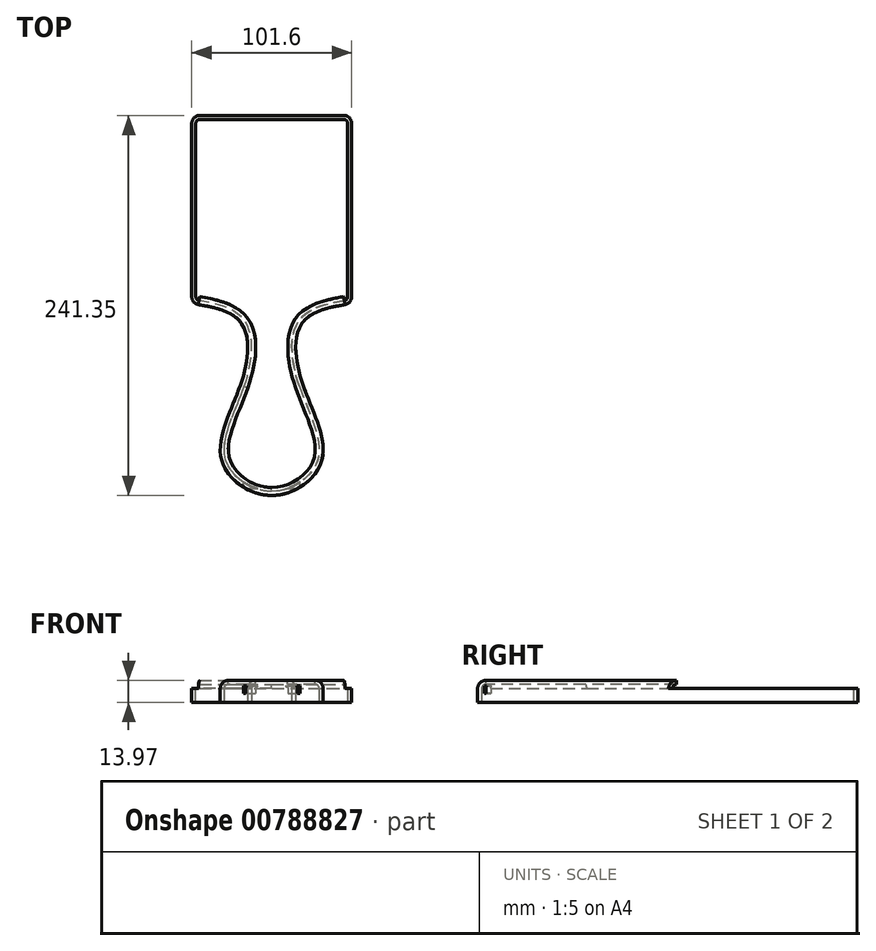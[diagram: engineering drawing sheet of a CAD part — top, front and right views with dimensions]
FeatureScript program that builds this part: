
annotation { "Feature Type Name" : "Feature", "Feature Type Description" : "" }
export const myFeature = defineFeature(function(context is Context, id is Id, definition is map)
    precondition{}
    {
        {
            var Q0;
            Q0=qCreatedBy(makeId("Top.planeOp"),FACE);
            var sketch = newSketch(context, id + "F0", { "sketchPlane" : qUnion([Q0])});
            skLineSegment(sketch, "E0.top", {"start": v(-50.8, -59.7) * mm, "end": v(50.8, -59.7) * mm});
            skLineSegment(sketch, "E1.bottom", {"start": v(-19.05, -59.7) * mm, "end": v(19.05, -59.7) * mm});
            skLineSegment(sketch, "E1.top", {"start": v(-19.05, -143.51) * mm, "end": v(19.05, -143.51) * mm});
            skLineSegment(sketch, "E2", {"start": v(-19.05, -59.69) * mm, "end": v(-138.22, -148.68) * mm, "construction": true});
            skPoint(sketch, "E3.4.internal.snap0", {"position": v(0, -143.51) * mm});
            skFitSpline(sketch, "E4", {"points": [v(31.98, -161.28) * mm, v(-138.22, -161.28) * mm], "startDerivative": vector(-191.75, -9.7) * mm, "endDerivative": vector(-168.23, 0) * mm, "construction": true});
            skFitSpline(sketch, "E5", {"points": [v(19.04, -111.52) * mm, v(-199.9, -111.52) * mm], "startDerivative": vector(-218.94, 0) * mm, "endDerivative": vector(-218.94, 0) * mm, "construction": true});
            skLineSegment(sketch, "E6", {"start": v(50.8, -59.7) * mm, "end": v(50.8, -228.04) * mm, "construction": true});
            skLineSegment(sketch, "E7", {"start": v(-50.8, -59.7) * mm, "end": v(-50.8, -228.04) * mm, "construction": true});
            skPoint(sketch, "E8", {"position": v(-44.45, -162.64) * mm});
            skPoint(sketch, "E9", {"position": v(31.8, -161.3) * mm});
            skLineSegment(sketch, "E10", {"start": v(0, -228.04) * mm, "end": v(0, -135.28) * mm});
            skPoint(sketch, "E11.orphan", {"position": v(0, -221.87) * mm});
            skLineSegment(sketch, "E12", {"start": v(-50.8, -59.7) * mm, "end": v(-50.8, 59.69) * mm});
            skLineSegment(sketch, "E13", {"start": v(-50.8, 59.69) * mm, "end": v(50.8, 59.69) * mm});
            skLineSegment(sketch, "E14", {"start": v(50.8, 59.7) * mm, "end": v(50.8, -59.7) * mm});
            skFitSpline(sketch, "E15", {"points": [v(-50.8, -59.7) * mm, v(-19.83, -71.53) * mm, v(-19.05, -108.97) * mm, v(-31.95, -158.73) * mm, v(0, -181.66) * mm, v(31.95, -158.73) * mm, v(19.05, -108.97) * mm, v(19.83, -71.53) * mm, v(50.8, -59.7) * mm], "startDerivative": vector(328.9, -55.01) * mm, "endDerivative": vector(328.9, 55.01) * mm});
            skFitSpline(sketch, "E16.MirrorCS", {"points": [v(50.8, -59.7) * mm, v(19.83, -71.53) * mm, v(19.05, -108.97) * mm, v(31.95, -158.73) * mm, v(0, -181.66) * mm, v(-31.95, -158.73) * mm, v(-19.05, -108.97) * mm, v(-19.83, -71.53) * mm, v(-50.8, -59.7) * mm], "startDerivative": vector(-328.9, -55.01) * mm, "endDerivative": vector(-328.9, 55.01) * mm});
            skLineSegment(sketch, "E17", {"start": v(0, -59.7) * mm, "end": v(0, 0) * mm, "construction": true});
            skLineSegment(sketch, "E18", {"start": v(-19.9, -111.52) * mm, "end": v(19.9, -111.52) * mm});
            skFitSpline(sketch, "E19", {"points": [v(31.98, -161.28) * mm, v(-138.22, -161.28) * mm], "startDerivative": vector(-191.75, -9.7) * mm, "endDerivative": vector(-168.23, 0) * mm, "construction": true});
            skFitSpline(sketch, "E20", {"points": [v(19.04, -111.52) * mm, v(-199.9, -111.52) * mm], "startDerivative": vector(-218.94, 0) * mm, "endDerivative": vector(-218.94, 0) * mm, "construction": true});
            skLineSegment(sketch, "E21", {"start": v(-50.8, 59.7) * mm, "end": v(50.8, 59.7) * mm});
            skFitSpline(sketch, "E22", {"points": [v(-50.8, -59.7) * mm, v(-19.83, -71.53) * mm, v(-19.05, -108.97) * mm, v(-31.95, -158.73) * mm, v(0, -181.66) * mm, v(31.95, -158.73) * mm, v(19.05, -108.97) * mm, v(19.83, -71.53) * mm, v(50.8, -59.7) * mm], "startDerivative": vector(328.9, -55.01) * mm, "endDerivative": vector(328.9, 55.01) * mm});
            skFitSpline(sketch, "E23.MirrorCS", {"points": [v(50.8, -59.7) * mm, v(19.83, -71.53) * mm, v(19.05, -108.97) * mm, v(31.95, -158.73) * mm, v(0, -181.66) * mm, v(-31.95, -158.73) * mm, v(-19.05, -108.97) * mm, v(-19.83, -71.53) * mm, v(-50.8, -59.7) * mm], "startDerivative": vector(-328.9, -55.01) * mm, "endDerivative": vector(-328.9, 55.01) * mm});
            skFitSpline(sketch, "E24", {"points": [v(-20.16, -129.65) * mm, v(-15.25, -116.48) * mm, v(-19.9, -111.52) * mm], "startDerivative": vector(14.14, 25.35) * mm, "endDerivative": vector(-15.4, 9.99) * mm});
            skFitSpline(sketch, "E25.MirrorCS", {"points": [v(20.16, -129.65) * mm, v(15.25, -116.48) * mm, v(19.9, -111.52) * mm], "startDerivative": vector(-14.14, 25.35) * mm, "endDerivative": vector(15.4, 9.99) * mm});
            skArc(sketch, "E26", {"start": v(-20.16, -129.65) * mm, "mid": v(0, -167.4) * mm, "end": v(20.16, -129.65) * mm});
            skSolve(sketch);
        }
        {
            var Q0;
            Q0 = qSketchRegion(id + "F0", true);
            extrude(context, id + "F1", {"entities" : qUnion([Q0]), "depth" : 19.05 * mm, "offsetDistance" : 25.4 * mm});
        }
        {
            var Q0;
            {var subQ0=sQuery(id+"F0.wireOp",EDGE,"619c9e35-8e4e-45b5-954f-d986f7143fad");Q0=makeQuery(id+"F1.opExtrude","CAP_EDGE",EDGE,{"disambiguationData":[OSD([subQ0]),TDD([makeQuery(id+"F0.imprint","IMPRINT",EDGE,{"disambiguationData":[TD([[makeQuery(id+"F0.imprint","INTERSECT",VERTEX,{"disambiguationData":[OD(0.0)],"derivedFrom":[sQuery(id+"F0.wireOp",EDGE,"cb9e0b87-6c60-422b-916c-469ffb9c9941.left"),subQ0]}),-1.0]])],"derivedFrom":subQ0})])],"isStart":false});}
            var Q1;
            {var subQ0=sQuery(id+"F0.wireOp",EDGE,"619c9e35-8e4e-45b5-954f-d986f7143fad");Q1=makeQuery(id+"F1.opExtrude","CAP_EDGE",EDGE,{"disambiguationData":[OSD([subQ0]),TDD([makeQuery(id+"F0.imprint","IMPRINT",EDGE,{"disambiguationData":[TD([[makeQuery(id+"F0.imprint","INTERSECT",VERTEX,{"disambiguationData":[OD(0.0)],"derivedFrom":[sQuery(id+"F0.wireOp",EDGE,"cb9e0b87-6c60-422b-916c-469ffb9c9941.right"),subQ0]}),1.0]])],"derivedFrom":subQ0})])],"isStart":false});}
            var Q2;
            {var subQ0=sQuery(id+"F0.wireOp",EDGE,"619c9e35-8e4e-45b5-954f-d986f7143fad");Q2=makeQuery(id+"F1.opExtrude","CAP_EDGE",EDGE,{"disambiguationData":[OSD([subQ0]),TDD([makeQuery(id+"F0.imprint","IMPRINT",EDGE,{"disambiguationData":[TD([[makeQuery(id+"F0.imprint","INTERSECT",VERTEX,{"disambiguationData":[OD(1.0)],"derivedFrom":[sQuery(id+"F0.wireOp",EDGE,"cb9e0b87-6c60-422b-916c-469ffb9c9941.left"),subQ0]}),1.0]])],"derivedFrom":subQ0})])],"isStart":false});}
            var Q3;
            Q3=makeQuery(id+"F1.opExtrude","CAP_EDGE",EDGE,{"disambiguationData":[OSD([sQuery(id+"F0.wireOp",EDGE,"cb9e0b87-6c60-422b-916c-469ffb9c9941.right")])],"isStart":false});
            var Q4;
            Q4=makeQuery(id+"F1.opExtrude","CAP_EDGE",EDGE,{"disambiguationData":[OSD([sQuery(id+"F0.wireOp",EDGE,"cb9e0b87-6c60-422b-916c-469ffb9c9941.left")])],"isStart":false});
            var Q5;
            Q5=makeQuery(id+"F1.opExtrude","CAP_EDGE",EDGE,{"disambiguationData":[OSD([sQuery(id+"F0.wireOp",EDGE,"abbb529c-c2db-4c8d-9435-7b284728a9ef.right")])],"isStart":false});
            var Q6;
            Q6=makeQuery(id+"F1.opExtrude","CAP_EDGE",EDGE,{"disambiguationData":[OSD([sQuery(id+"F0.wireOp",EDGE,"abbb529c-c2db-4c8d-9435-7b284728a9ef.left")])],"isStart":false});
            var Q7;
            Q7=makeQuery(id+"F1.opExtrude","CAP_EDGE",EDGE,{"disambiguationData":[OSD([sQuery(id+"F0.wireOp",EDGE,"abbb529c-c2db-4c8d-9435-7b284728a9ef.bottom")])],"isStart":false});
            var Q8;
            {var subQ0=sQuery(id+"F0.wireOp",EDGE,"619c9e35-8e4e-45b5-954f-d986f7143fad");Q8=makeQuery(id+"F1.opExtrude","CAP_EDGE",EDGE,{"disambiguationData":[OSD([subQ0]),TDD([makeQuery(id+"F0.imprint","IMPRINT",EDGE,{"disambiguationData":[TD([[makeQuery(id+"F0.imprint","INTERSECT",VERTEX,{"disambiguationData":[OD(1.0)],"derivedFrom":[sQuery(id+"F0.wireOp",EDGE,"cb9e0b87-6c60-422b-916c-469ffb9c9941.left"),subQ0]}),1.0]])],"derivedFrom":subQ0})])],"isStart":true});}
            var Q9;
            {var subQ0=sQuery(id+"F0.wireOp",EDGE,"619c9e35-8e4e-45b5-954f-d986f7143fad");Q9=makeQuery(id+"F1.opExtrude","CAP_EDGE",EDGE,{"disambiguationData":[OSD([subQ0]),TDD([makeQuery(id+"F0.imprint","IMPRINT",EDGE,{"disambiguationData":[TD([[makeQuery(id+"F0.imprint","INTERSECT",VERTEX,{"disambiguationData":[OD(0.0)],"derivedFrom":[sQuery(id+"F0.wireOp",EDGE,"cb9e0b87-6c60-422b-916c-469ffb9c9941.left"),subQ0]}),-1.0]])],"derivedFrom":subQ0})])],"isStart":true});}
            var Q10;
            Q10=makeQuery(id+"F1.opExtrude","CAP_EDGE",EDGE,{"disambiguationData":[OSD([sQuery(id+"F0.wireOp",EDGE,"abbb529c-c2db-4c8d-9435-7b284728a9ef.bottom")])],"isStart":true});
            var Q11;
            {var subQ0=sQuery(id+"F0.wireOp",EDGE,"619c9e35-8e4e-45b5-954f-d986f7143fad");Q11=makeQuery(id+"F1.opExtrude","CAP_EDGE",EDGE,{"disambiguationData":[OSD([subQ0]),TDD([makeQuery(id+"F0.imprint","IMPRINT",EDGE,{"disambiguationData":[TD([[makeQuery(id+"F0.imprint","INTERSECT",VERTEX,{"disambiguationData":[OD(0.0)],"derivedFrom":[sQuery(id+"F0.wireOp",EDGE,"cb9e0b87-6c60-422b-916c-469ffb9c9941.right"),subQ0]}),1.0]])],"derivedFrom":subQ0})])],"isStart":true});}
            var Q12;
            Q12=makeQuery(id+"F1.opExtrude","SWEPT_EDGE",EDGE,{"disambiguationData":[OSD([sQuery(id+"F0.wireOp",EDGE,"abbb529c-c2db-4c8d-9435-7b284728a9ef.top"),sQuery(id+"F0.wireOp",EDGE,"abbb529c-c2db-4c8d-9435-7b284728a9ef.right"),sQuery(id+"F0.wireOp",EDGE,"619c9e35-8e4e-45b5-954f-d986f7143fad")])]});
            var Q13;
            Q13=makeQuery(id+"F1.opExtrude","SWEPT_EDGE",EDGE,{"disambiguationData":[OSD([sQuery(id+"F0.wireOp",EDGE,"abbb529c-c2db-4c8d-9435-7b284728a9ef.top"),sQuery(id+"F0.wireOp",EDGE,"abbb529c-c2db-4c8d-9435-7b284728a9ef.left"),sQuery(id+"F0.wireOp",EDGE,"619c9e35-8e4e-45b5-954f-d986f7143fad")])]});
            var Q14;
            Q14=makeQuery(id+"F1.opExtrude","SWEPT_EDGE",EDGE,{"disambiguationData":[OSD([sQuery(id+"F0.wireOp",EDGE,"abbb529c-c2db-4c8d-9435-7b284728a9ef.bottom"),sQuery(id+"F0.wireOp",EDGE,"abbb529c-c2db-4c8d-9435-7b284728a9ef.left")])]});
            var Q15;
            {var subQ0=sQuery(id+"F0.wireOp",EDGE,"619c9e35-8e4e-45b5-954f-d986f7143fad");var subQ1=sQuery(id+"F0.wireOp",EDGE,"cb9e0b87-6c60-422b-916c-469ffb9c9941.left");Q15=makeQuery(id+"F1.opExtrude","SWEPT_EDGE",EDGE,{"disambiguationData":[OSD([subQ1,subQ0]),TDD([makeQuery(id+"F0.imprint","INTERSECT",VERTEX,{"disambiguationData":[OD(0.0)],"derivedFrom":[subQ1,subQ0]})])]});}
            var Q16;
            {var subQ0=sQuery(id+"F0.wireOp",EDGE,"619c9e35-8e4e-45b5-954f-d986f7143fad");var subQ1=sQuery(id+"F0.wireOp",EDGE,"cb9e0b87-6c60-422b-916c-469ffb9c9941.left");Q16=makeQuery(id+"F1.opExtrude","SWEPT_EDGE",EDGE,{"disambiguationData":[OSD([subQ1,subQ0]),TDD([makeQuery(id+"F0.imprint","INTERSECT",VERTEX,{"disambiguationData":[OD(1.0)],"derivedFrom":[subQ1,subQ0]})])]});}
            var Q17;
            Q17=makeQuery(id+"F1.opExtrude","CAP_EDGE",EDGE,{"disambiguationData":[OSD([sQuery(id+"F0.wireOp",EDGE,"abbb529c-c2db-4c8d-9435-7b284728a9ef.right")])],"isStart":true});
            var Q18;
            Q18=makeQuery(id+"F1.opExtrude","CAP_EDGE",EDGE,{"disambiguationData":[OSD([sQuery(id+"F0.wireOp",EDGE,"abbb529c-c2db-4c8d-9435-7b284728a9ef.left")])],"isStart":true});
            var Q19;
            {var subQ0=sQuery(id+"F0.wireOp",EDGE,"619c9e35-8e4e-45b5-954f-d986f7143fad");var subQ1=sQuery(id+"F0.wireOp",EDGE,"cb9e0b87-6c60-422b-916c-469ffb9c9941.right");Q19=makeQuery(id+"F1.opExtrude","SWEPT_EDGE",EDGE,{"disambiguationData":[OSD([subQ1,subQ0]),TDD([makeQuery(id+"F0.imprint","INTERSECT",VERTEX,{"disambiguationData":[OD(0.0)],"derivedFrom":[subQ1,subQ0]})])]});}
            var Q20;
            {var subQ0=sQuery(id+"F0.wireOp",EDGE,"619c9e35-8e4e-45b5-954f-d986f7143fad");var subQ1=sQuery(id+"F0.wireOp",EDGE,"cb9e0b87-6c60-422b-916c-469ffb9c9941.right");Q20=makeQuery(id+"F1.opExtrude","SWEPT_EDGE",EDGE,{"disambiguationData":[OSD([subQ1,subQ0]),TDD([makeQuery(id+"F0.imprint","INTERSECT",VERTEX,{"disambiguationData":[OD(1.0)],"derivedFrom":[subQ1,subQ0]})])]});}
            var Q21;
            Q21=makeQuery(id+"F1.opExtrude","CAP_EDGE",EDGE,{"disambiguationData":[OSD([sQuery(id+"F0.wireOp",EDGE,"cb9e0b87-6c60-422b-916c-469ffb9c9941.right")])],"isStart":true});
            var Q22;
            Q22=makeQuery(id+"F1.opExtrude","CAP_EDGE",EDGE,{"disambiguationData":[OSD([sQuery(id+"F0.wireOp",EDGE,"cb9e0b87-6c60-422b-916c-469ffb9c9941.left")])],"isStart":true});
            var Q23;
            Q23=makeQuery(id+"F1.opExtrude","SWEPT_EDGE",EDGE,{"disambiguationData":[OSD([sQuery(id+"F0.wireOp",EDGE,"abbb529c-c2db-4c8d-9435-7b284728a9ef.bottom"),sQuery(id+"F0.wireOp",EDGE,"abbb529c-c2db-4c8d-9435-7b284728a9ef.right")])]});
            var Q24;
            Q24=makeQuery(id+"F1.opExtrude","CAP_EDGE",EDGE,{"disambiguationData":[OSD([sQuery(id+"F0.wireOp",EDGE,"4c9936b5-c191-433f-b99c-079e70b91c7e.right")])],"isStart":false});
            var Q25;
            Q25=makeQuery(id+"F1.opExtrude","CAP_EDGE",EDGE,{"disambiguationData":[OSD([sQuery(id+"F0.wireOp",EDGE,"bdb519ba-7cbe-487b-a66f-37edebb15bfe.MirrorCS")])],"isStart":false});
            var Q26;
            Q26=makeQuery(id+"F1.opExtrude","SWEPT_EDGE",EDGE,{"disambiguationData":[OSD([sQuery(id+"F0.wireOp",EDGE,"4c9936b5-c191-433f-b99c-079e70b91c7e.bottom"),sQuery(id+"F0.wireOp",EDGE,"4c9936b5-c191-433f-b99c-079e70b91c7e.right")])]});
            var Q27;
            Q27=makeQuery(id+"F1.opExtrude","CAP_EDGE",EDGE,{"disambiguationData":[OSD([sQuery(id+"F0.wireOp",EDGE,"4c9936b5-c191-433f-b99c-079e70b91c7e.bottom")])],"isStart":false});
            var Q28;
            Q28=makeQuery(id+"F1.opExtrude","CAP_EDGE",EDGE,{"disambiguationData":[OSD([sQuery(id+"F0.wireOp",EDGE,"4c9936b5-c191-433f-b99c-079e70b91c7e.left")])],"isStart":false});
            var Q29;
            Q29=makeQuery(id+"F1.opExtrude","CAP_EDGE",EDGE,{"disambiguationData":[OSD([sQuery(id+"F0.wireOp",EDGE,"2c6a8658-700c-4ae6-8bb7-a65d1a4c6f69")])],"isStart":false});
            var Q30;
            Q30=makeQuery(id+"F1.opExtrude","CAP_EDGE",EDGE,{"disambiguationData":[OSD([sQuery(id+"F0.wireOp",EDGE,"4c9936b5-c191-433f-b99c-079e70b91c7e.right")])],"isStart":true});
            var Q31;
            Q31=makeQuery(id+"F1.opExtrude","SWEPT_EDGE",EDGE,{"disambiguationData":[OSD([sQuery(id+"F0.wireOp",EDGE,"4c9936b5-c191-433f-b99c-079e70b91c7e.top"),sQuery(id+"F0.wireOp",EDGE,"4c9936b5-c191-433f-b99c-079e70b91c7e.right"),sQuery(id+"F0.wireOp",EDGE,"bdb519ba-7cbe-487b-a66f-37edebb15bfe.MirrorCS")])]});
            var Q32;
            Q32=makeQuery(id+"F1.opExtrude","CAP_FACE",FACE,{"disambiguationData":[OSD([sQuery(id+"F0.wireOp",EDGE,"4c9936b5-c191-433f-b99c-079e70b91c7e.bottom"),sQuery(id+"F0.wireOp",EDGE,"4c9936b5-c191-433f-b99c-079e70b91c7e.left"),sQuery(id+"F0.wireOp",EDGE,"4c9936b5-c191-433f-b99c-079e70b91c7e.right"),sQuery(id+"F0.wireOp",EDGE,"2c6a8658-700c-4ae6-8bb7-a65d1a4c6f69"),sQuery(id+"F0.wireOp",EDGE,"bdb519ba-7cbe-487b-a66f-37edebb15bfe.MirrorCS")])],"isStart":true});
            var Q33;
            Q33=makeQuery(id+"F1.opExtrude","SWEPT_EDGE",EDGE,{"disambiguationData":[OSD([sQuery(id+"F0.wireOp",EDGE,"4c9936b5-c191-433f-b99c-079e70b91c7e.bottom"),sQuery(id+"F0.wireOp",EDGE,"4c9936b5-c191-433f-b99c-079e70b91c7e.left")])]});
            var Q34;
            Q34=makeQuery(id+"F1.opExtrude","SWEPT_EDGE",EDGE,{"disambiguationData":[OSD([sQuery(id+"F0.wireOp",EDGE,"4c9936b5-c191-433f-b99c-079e70b91c7e.top"),sQuery(id+"F0.wireOp",EDGE,"4c9936b5-c191-433f-b99c-079e70b91c7e.left"),sQuery(id+"F0.wireOp",EDGE,"2c6a8658-700c-4ae6-8bb7-a65d1a4c6f69")])]});
            var Q35;
            Q35=makeQuery(id+"F1.opExtrude","SWEPT_EDGE",EDGE,{"disambiguationData":[OSD([sQuery(id+"F0.wireOp",EDGE,"2c6a8658-700c-4ae6-8bb7-a65d1a4c6f69"),sQuery(id+"F0.wireOp",EDGE,"bdb519ba-7cbe-487b-a66f-37edebb15bfe.MirrorCS")])]});
            var Q36;
            Q36=makeQuery(id+"F1.opExtrude","SWEPT_EDGE",EDGE,{"disambiguationData":[OSD([sQuery(id+"F0.wireOp",EDGE,"c34ce0ff-0ec7-4ae9-b71e-ae422a1ad343"),sQuery(id+"F0.wireOp",EDGE,"30933a0e-8d92-4604-b30c-e4b37162de66")])]});
            var Q37;
            Q37=makeQuery(id+"F1.opExtrude","CAP_EDGE",EDGE,{"disambiguationData":[OSD([sQuery(id+"F0.wireOp",EDGE,"30933a0e-8d92-4604-b30c-e4b37162de66")])],"isStart":false});
            var Q38;
            Q38=makeQuery(id+"F1.opExtrude","CAP_EDGE",EDGE,{"disambiguationData":[OSD([sQuery(id+"F0.wireOp",EDGE,"c34ce0ff-0ec7-4ae9-b71e-ae422a1ad343")])],"isStart":false});
            var Q39;
            Q39=makeQuery(id+"F1.opExtrude","CAP_EDGE",EDGE,{"disambiguationData":[OSD([sQuery(id+"F0.wireOp",EDGE,"c34ce0ff-0ec7-4ae9-b71e-ae422a1ad343")])],"isStart":true});
            var Q40;
            Q40=makeQuery(id+"F1.opExtrude","CAP_EDGE",EDGE,{"disambiguationData":[OSD([sQuery(id+"F0.wireOp",EDGE,"30933a0e-8d92-4604-b30c-e4b37162de66")])],"isStart":true});
            var Q41;
            Q41=makeQuery(id+"F1.opExtrude","CAP_EDGE",EDGE,{"disambiguationData":[OSD([sQuery(id+"F0.wireOp",EDGE,"5cded980-a9cc-4845-a9e5-2a2afa72b9e1.MirrorCS")])],"isStart":true});
            var Q42;
            Q42=makeQuery(id+"F1.opExtrude","SWEPT_EDGE",EDGE,{"disambiguationData":[OSD([sQuery(id+"F0.wireOp",EDGE,"e66cdaa8-c890-470a-b91a-6813027ddbfc.top"),sQuery(id+"F0.wireOp",EDGE,"dfdcc702-bab6-440e-817f-0e8d2b34580e"),sQuery(id+"F0.wireOp",EDGE,"9f91019e-6544-4331-85e9-98c714eb1747")])]});
            var Q43;
            Q43=makeQuery(id+"F1.opExtrude","CAP_EDGE",EDGE,{"disambiguationData":[OSD([sQuery(id+"F0.wireOp",EDGE,"9f91019e-6544-4331-85e9-98c714eb1747")])],"isStart":true});
            var Q44;
            Q44=makeQuery(id+"F1.opExtrude","CAP_EDGE",EDGE,{"disambiguationData":[OSD([sQuery(id+"F0.wireOp",EDGE,"9f91019e-6544-4331-85e9-98c714eb1747")])],"isStart":false});
            var Q45;
            Q45=makeQuery(id+"F1.opExtrude","SWEPT_EDGE",EDGE,{"disambiguationData":[OSD([sQuery(id+"F0.wireOp",EDGE,"e66cdaa8-c890-470a-b91a-6813027ddbfc.top"),sQuery(id+"F0.wireOp",EDGE,"5cded980-a9cc-4845-a9e5-2a2afa72b9e1.MirrorCS"),sQuery(id+"F0.wireOp",EDGE,"30933a0e-8d92-4604-b30c-e4b37162de66")])]});
            var Q46;
            Q46=makeQuery(id+"F1.opExtrude","CAP_EDGE",EDGE,{"disambiguationData":[OSD([sQuery(id+"F0.wireOp",EDGE,"dfdcc702-bab6-440e-817f-0e8d2b34580e")])],"isStart":true});
            var Q47;
            Q47=makeQuery(id+"F1.opExtrude","CAP_EDGE",EDGE,{"disambiguationData":[OSD([sQuery(id+"F0.wireOp",EDGE,"5cded980-a9cc-4845-a9e5-2a2afa72b9e1.MirrorCS")])],"isStart":false});
            var Q48;
            Q48=makeQuery(id+"F1.opExtrude","CAP_EDGE",EDGE,{"disambiguationData":[OSD([sQuery(id+"F0.wireOp",EDGE,"dfdcc702-bab6-440e-817f-0e8d2b34580e")])],"isStart":false});
            var Q49;
            Q49=makeQuery(id+"F1.opExtrude","SWEPT_EDGE",EDGE,{"disambiguationData":[OSD([sQuery(id+"F0.wireOp",EDGE,"9f91019e-6544-4331-85e9-98c714eb1747"),sQuery(id+"F0.wireOp",EDGE,"c34ce0ff-0ec7-4ae9-b71e-ae422a1ad343")])]});
            var Q50;
            Q50=makeQuery(id+"F1.opExtrude","CAP_EDGE",EDGE,{"disambiguationData":[OSD([sQuery(id+"F0.wireOp",EDGE,"74c69ee1-55aa-481c-bcd1-1569f91f6e900.MirrorCS")])],"isStart":false});
            var Q51;
            Q51=makeQuery(id+"F1.opExtrude","CAP_EDGE",EDGE,{"disambiguationData":[OSD([sQuery(id+"F0.wireOp",EDGE,"03ce3f70-f8f5-48b6-817a-86b3da3b079a")])],"isStart":false});
            var Q52;
            Q52=makeQuery(id+"F1.opExtrude","CAP_EDGE",EDGE,{"disambiguationData":[OSD([sQuery(id+"F0.wireOp",EDGE,"7e58dfbd-d96a-4cb8-ae05-f5717cad55f7")])],"isStart":false});
            var Q53;
            Q53=makeQuery(id+"F1.opExtrude","CAP_EDGE",EDGE,{"disambiguationData":[OSD([sQuery(id+"F0.wireOp",EDGE,"be0bfd59-5de7-4c36-b741-230e249a2633")])],"isStart":false});
            var Q54;
            Q54=makeQuery(id+"F1.opExtrude","CAP_EDGE",EDGE,{"disambiguationData":[OSD([sQuery(id+"F0.wireOp",EDGE,"bf2bad3a-775d-4bb9-9518-0aa501403ff7")])],"isStart":false});
            var Q55;
            Q55=makeQuery(id+"F1.opExtrude","CAP_EDGE",EDGE,{"disambiguationData":[OSD([sQuery(id+"F0.wireOp",EDGE,"74c69ee1-55aa-481c-bcd1-1569f91f6e900.MirrorCS")])],"isStart":true});
            var Q56;
            Q56=makeQuery(id+"F1.opExtrude","CAP_EDGE",EDGE,{"disambiguationData":[OSD([sQuery(id+"F0.wireOp",EDGE,"03ce3f70-f8f5-48b6-817a-86b3da3b079a")])],"isStart":true});
            var Q57;
            Q57=makeQuery(id+"F1.opExtrude","CAP_EDGE",EDGE,{"disambiguationData":[OSD([sQuery(id+"F0.wireOp",EDGE,"7e58dfbd-d96a-4cb8-ae05-f5717cad55f7")])],"isStart":true});
            var Q58;
            Q58=makeQuery(id+"F1.opExtrude","CAP_EDGE",EDGE,{"disambiguationData":[OSD([sQuery(id+"F0.wireOp",EDGE,"be0bfd59-5de7-4c36-b741-230e249a2633")])],"isStart":true});
            var Q59;
            Q59=makeQuery(id+"F1.opExtrude","SWEPT_EDGE",EDGE,{"disambiguationData":[OSD([sQuery(id+"F0.wireOp",EDGE,"c97fd30b-f4b9-4084-8bae-b5abf99d8afd.top"),sQuery(id+"F0.wireOp",EDGE,"03ce3f70-f8f5-48b6-817a-86b3da3b079a"),sQuery(id+"F0.wireOp",EDGE,"74c69ee1-55aa-481c-bcd1-1569f91f6e900.MirrorCS")])]});
            var Q60;
            Q60=makeQuery(id+"F1.opExtrude","SWEPT_EDGE",EDGE,{"disambiguationData":[OSD([sQuery(id+"F0.wireOp",EDGE,"be0bfd59-5de7-4c36-b741-230e249a2633"),sQuery(id+"F0.wireOp",EDGE,"03ce3f70-f8f5-48b6-817a-86b3da3b079a")])]});
            var Q61;
            Q61=makeQuery(id+"F1.opExtrude","SWEPT_EDGE",EDGE,{"disambiguationData":[OSD([sQuery(id+"F0.wireOp",EDGE,"7e58dfbd-d96a-4cb8-ae05-f5717cad55f7"),sQuery(id+"F0.wireOp",EDGE,"be0bfd59-5de7-4c36-b741-230e249a2633")])]});
            var Q62;
            Q62=makeQuery(id+"F1.opExtrude","SWEPT_EDGE",EDGE,{"disambiguationData":[OSD([sQuery(id+"F0.wireOp",EDGE,"c97fd30b-f4b9-4084-8bae-b5abf99d8afd.top"),sQuery(id+"F0.wireOp",EDGE,"7e58dfbd-d96a-4cb8-ae05-f5717cad55f7"),sQuery(id+"F0.wireOp",EDGE,"bf2bad3a-775d-4bb9-9518-0aa501403ff7")])]});
            var Q63;
            Q63=makeQuery(id+"F1.opExtrude","CAP_EDGE",EDGE,{"disambiguationData":[OSD([sQuery(id+"F0.wireOp",EDGE,"E15"),sQuery(id+"F0.wireOp",EDGE,"E16.MirrorCS")])],"isStart":false});
            var Q64;
            Q64=makeQuery(id+"F1.opExtrude","CAP_FACE",FACE,{"disambiguationData":[OSD([sQuery(id+"F0.wireOp",EDGE,"E12"),sQuery(id+"F0.wireOp",EDGE,"E13"),sQuery(id+"F0.wireOp",EDGE,"E14"),sQuery(id+"F0.wireOp",EDGE,"E15"),sQuery(id+"F0.wireOp",EDGE,"E16.MirrorCS")])],"isStart":false});
            var Q65;
            Q65=makeQuery(id+"F1.opExtrude","CAP_FACE",FACE,{"disambiguationData":[OSD([sQuery(id+"F0.wireOp",EDGE,"E12"),sQuery(id+"F0.wireOp",EDGE,"E13"),sQuery(id+"F0.wireOp",EDGE,"E14"),sQuery(id+"F0.wireOp",EDGE,"E15"),sQuery(id+"F0.wireOp",EDGE,"E16.MirrorCS")])],"isStart":true});
            var Q66;
            Q66=makeQuery(id+"F1.opExtrude","SWEPT_EDGE",EDGE,{"disambiguationData":[OSD([sQuery(id+"F0.wireOp",EDGE,"E13"),sQuery(id+"F0.wireOp",EDGE,"E14")])]});
            var Q67;
            Q67=makeQuery(id+"F1.opExtrude","SWEPT_EDGE",EDGE,{"disambiguationData":[OSD([sQuery(id+"F0.wireOp",EDGE,"E0.top"),sQuery(id+"F0.wireOp",EDGE,"E14"),sQuery(id+"F0.wireOp",EDGE,"E16.MirrorCS")])]});
            var Q68;
            Q68=makeQuery(id+"F1.opExtrude","SWEPT_EDGE",EDGE,{"disambiguationData":[OSD([sQuery(id+"F0.wireOp",EDGE,"E0.top"),sQuery(id+"F0.wireOp",EDGE,"E12"),sQuery(id+"F0.wireOp",EDGE,"E15")])]});
            var Q69;
            Q69=makeQuery(id+"F1.opExtrude","SWEPT_EDGE",EDGE,{"disambiguationData":[OSD([sQuery(id+"F0.wireOp",EDGE,"E12"),sQuery(id+"F0.wireOp",EDGE,"E13")])]});
            var Q70;
            Q70=makeQuery(id+"F1.opExtrude","CAP_EDGE",EDGE,{"disambiguationData":[OSD([sQuery(id+"F0.wireOp",EDGE,"E21")])],"isStart":false});
            var Q71;
            Q71=makeQuery(id+"F1.opExtrude","CAP_EDGE",EDGE,{"disambiguationData":[OSD([sQuery(id+"F0.wireOp",EDGE,"E14")])],"isStart":false});
            var Q72;
            Q72=makeQuery(id+"F1.opExtrude","CAP_EDGE",EDGE,{"disambiguationData":[OSD([sQuery(id+"F0.wireOp",EDGE,"E12")])],"isStart":false});
            var Q73;
            Q73=makeQuery(id+"F1.opExtrude","CAP_EDGE",EDGE,{"disambiguationData":[OSD([sQuery(id+"F0.wireOp",EDGE,"E22")])],"isStart":false});
            var Q74;
            Q74=makeQuery(id+"F1.opExtrude","CAP_EDGE",EDGE,{"disambiguationData":[OSD([sQuery(id+"F0.wireOp",EDGE,"E23.MirrorCS")])],"isStart":false});
            var Q75;
            Q75=makeQuery(id+"F1.opExtrude","CAP_EDGE",EDGE,{"disambiguationData":[OSD([sQuery(id+"F0.wireOp",EDGE,"E26")])],"isStart":false});
            var Q76;
            Q76=makeQuery(id+"F1.opExtrude","CAP_EDGE",EDGE,{"disambiguationData":[OSD([sQuery(id+"F0.wireOp",EDGE,"E23.MirrorCS")])],"isStart":true});
            var Q77;
            Q77=makeQuery(id+"F1.opExtrude","CAP_EDGE",EDGE,{"disambiguationData":[OSD([sQuery(id+"F0.wireOp",EDGE,"E25.MirrorCS")])],"isStart":true});
            var Q78;
            Q78=makeQuery(id+"F1.opExtrude","CAP_EDGE",EDGE,{"disambiguationData":[OSD([sQuery(id+"F0.wireOp",EDGE,"E26")])],"isStart":true});
            var Q79;
            Q79=makeQuery(id+"F1.opExtrude","SWEPT_EDGE",EDGE,{"disambiguationData":[OSD([sQuery(id+"F0.wireOp",EDGE,"E0.top"),sQuery(id+"F0.wireOp",EDGE,"E14"),sQuery(id+"F0.wireOp",EDGE,"E23.MirrorCS")])]});
            var Q80;
            Q80=makeQuery(id+"F1.opExtrude","SWEPT_EDGE",EDGE,{"disambiguationData":[OSD([sQuery(id+"F0.wireOp",EDGE,"E18"),sQuery(id+"F0.wireOp",EDGE,"E23.MirrorCS"),sQuery(id+"F0.wireOp",EDGE,"E25.MirrorCS")])]});
            var Q81;
            Q81=makeQuery(id+"F1.opExtrude","SWEPT_EDGE",EDGE,{"disambiguationData":[OSD([sQuery(id+"F0.wireOp",EDGE,"E25.MirrorCS"),sQuery(id+"F0.wireOp",EDGE,"E26")])]});
            var Q82;
            Q82=makeQuery(id+"F1.opExtrude","SWEPT_EDGE",EDGE,{"disambiguationData":[OSD([sQuery(id+"F0.wireOp",EDGE,"E18"),sQuery(id+"F0.wireOp",EDGE,"E22"),sQuery(id+"F0.wireOp",EDGE,"E24")])]});
            var Q83;
            Q83=makeQuery(id+"F1.opExtrude","CAP_EDGE",EDGE,{"disambiguationData":[OSD([sQuery(id+"F0.wireOp",EDGE,"E24")])],"isStart":true});
            var Q84;
            Q84=makeQuery(id+"F1.opExtrude","SWEPT_EDGE",EDGE,{"disambiguationData":[OSD([sQuery(id+"F0.wireOp",EDGE,"E24"),sQuery(id+"F0.wireOp",EDGE,"E26")])]});
            var Q85;
            Q85=makeQuery(id+"F1.opExtrude","CAP_EDGE",EDGE,{"disambiguationData":[OSD([sQuery(id+"F0.wireOp",EDGE,"E22")])],"isStart":true});
            var Q86;
            Q86=makeQuery(id+"F1.opExtrude","SWEPT_EDGE",EDGE,{"disambiguationData":[OSD([sQuery(id+"F0.wireOp",EDGE,"E0.top"),sQuery(id+"F0.wireOp",EDGE,"E12"),sQuery(id+"F0.wireOp",EDGE,"E22")])]});
            var Q87;
            Q87=makeQuery(id+"F1.opExtrude","CAP_EDGE",EDGE,{"disambiguationData":[OSD([sQuery(id+"F0.wireOp",EDGE,"E12")])],"isStart":true});
            var Q88;
            Q88=makeQuery(id+"F1.opExtrude","SWEPT_EDGE",EDGE,{"disambiguationData":[OSD([sQuery(id+"F0.wireOp",EDGE,"E12"),sQuery(id+"F0.wireOp",EDGE,"E21")])]});
            var Q89;
            Q89=makeQuery(id+"F1.opExtrude","SWEPT_EDGE",EDGE,{"disambiguationData":[OSD([sQuery(id+"F0.wireOp",EDGE,"E21"),sQuery(id+"F0.wireOp",EDGE,"E14")])]});
            var Q90;
            Q90=makeQuery(id+"F1.opExtrude","CAP_EDGE",EDGE,{"disambiguationData":[OSD([sQuery(id+"F0.wireOp",EDGE,"E14")])],"isStart":true});
            var Q91;
            Q91=makeQuery(id+"F1.opExtrude","CAP_EDGE",EDGE,{"disambiguationData":[OSD([sQuery(id+"F0.wireOp",EDGE,"E21")])],"isStart":true});
            fillet(context, id + "F2", {"entities" : qUnion([Q0, Q1, Q2, Q3, Q4, Q5, Q6, Q7, Q8, Q9, Q10, Q11, Q12, Q13, Q14, Q15, Q16, Q17, Q18, Q19, Q20, Q21, Q22, Q23, Q24, Q25, Q26, Q27, Q28, Q29, Q30, Q31, Q32, Q33, Q34, Q35, Q36, Q37, Q38, Q39, Q40, Q41, Q42, Q43, Q44, Q45, Q46, Q47, Q48, Q49, Q50, Q51, Q52, Q53, Q54, Q55, Q56, Q57, Q58, Q59, Q60, Q61, Q62, Q63, Q64, Q65, Q66, Q67, Q68, Q69, Q70, Q71, Q72, Q73, Q74, Q75, Q76, Q77, Q78, Q79, Q80, Q81, Q82, Q83, Q84, Q85, Q86, Q87, Q88, Q89, Q90, Q91]), "radius" : 5.08 * mm, "tangentPropagation" : true, "allowEdgeOverflow" : false});
        }
        {
            var Q0;
            Q0=qCreatedBy(makeId("Top.planeOp"),FACE);
            var sketch = newSketch(context, id + "F3", { "sketchPlane" : qUnion([Q0])});
            skLineSegment(sketch, "E27", {"start": v(-45.62, 55) * mm, "end": v(45.76, 55) * mm});
            skCircle(sketch, "E28", {"center": v(-42.67, 52.68) * mm, "radius": 0.64 * mm});
            skCircle(sketch, "E29.1.0.0", {"center": v(-39.12, 52.68) * mm, "radius": 0.64 * mm});
            skCircle(sketch, "E29.2.0.0", {"center": v(-35.56, 52.68) * mm, "radius": 0.64 * mm});
            skCircle(sketch, "E29.3.0.0", {"center": v(-32, 52.68) * mm, "radius": 0.64 * mm});
            skCircle(sketch, "E29.4.0.0", {"center": v(-28.45, 52.68) * mm, "radius": 0.64 * mm});
            skCircle(sketch, "E29.5.0.0", {"center": v(-24.9, 52.68) * mm, "radius": 0.64 * mm});
            skCircle(sketch, "E29.6.0.0", {"center": v(-21.34, 52.68) * mm, "radius": 0.64 * mm});
            skCircle(sketch, "E29.7.0.0", {"center": v(-17.78, 52.68) * mm, "radius": 0.64 * mm});
            skCircle(sketch, "E29.8.0.0", {"center": v(-14.22, 52.68) * mm, "radius": 0.64 * mm});
            skCircle(sketch, "E29.9.0.0", {"center": v(-10.67, 52.68) * mm, "radius": 0.64 * mm});
            skCircle(sketch, "E29.10.0.0", {"center": v(-7.11, 52.68) * mm, "radius": 0.64 * mm});
            skCircle(sketch, "E29.11.0.0", {"center": v(-3.56, 52.68) * mm, "radius": 0.64 * mm});
            skCircle(sketch, "E29.12.0.0", {"center": v(0, 52.68) * mm, "radius": 0.64 * mm});
            skCircle(sketch, "E29.13.0.0", {"center": v(3.56, 52.68) * mm, "radius": 0.64 * mm});
            skCircle(sketch, "E29.14.0.0", {"center": v(7.11, 52.68) * mm, "radius": 0.64 * mm});
            skCircle(sketch, "E29.15.0.0", {"center": v(10.67, 52.68) * mm, "radius": 0.64 * mm});
            skCircle(sketch, "E29.16.0.0", {"center": v(14.22, 52.68) * mm, "radius": 0.64 * mm});
            skCircle(sketch, "E29.17.0.0", {"center": v(17.78, 52.68) * mm, "radius": 0.64 * mm});
            skCircle(sketch, "E29.18.0.0", {"center": v(21.34, 52.68) * mm, "radius": 0.64 * mm});
            skCircle(sketch, "E29.19.0.0", {"center": v(24.9, 52.68) * mm, "radius": 0.64 * mm});
            skLineSegment(sketch, "E29.direction1", {"start": v(-42.67, 52.68) * mm, "end": v(-39.12, 52.68) * mm, "construction": true});
            skCircle(sketch, "E30.0.20.0", {"center": v(28.45, 52.68) * mm, "radius": 0.64 * mm});
            skCircle(sketch, "E30.0.21.0", {"center": v(32, 52.68) * mm, "radius": 0.64 * mm});
            skCircle(sketch, "E30.0.22.0", {"center": v(35.56, 52.68) * mm, "radius": 0.64 * mm});
            skCircle(sketch, "E30.0.23.0", {"center": v(39.12, 52.68) * mm, "radius": 0.64 * mm});
            skCircle(sketch, "E31.0.24.0", {"center": v(42.67, 52.68) * mm, "radius": 0.64 * mm});
            skCircle(sketch, "E32.1.0.0", {"center": v(39.12, 49.02) * mm, "radius": 0.64 * mm});
            skCircle(sketch, "E32.1.0.1", {"center": v(14.22, 49.02) * mm, "radius": 0.64 * mm});
            skCircle(sketch, "E32.1.0.2", {"center": v(-32, 49.02) * mm, "radius": 0.64 * mm});
            skCircle(sketch, "E32.1.0.3", {"center": v(10.67, 49.02) * mm, "radius": 0.64 * mm});
            skCircle(sketch, "E32.1.0.4", {"center": v(-35.56, 49.02) * mm, "radius": 0.64 * mm});
            skCircle(sketch, "E32.1.0.5", {"center": v(17.78, 49.02) * mm, "radius": 0.64 * mm});
            skCircle(sketch, "E32.1.0.6", {"center": v(3.56, 49.02) * mm, "radius": 0.64 * mm});
            skCircle(sketch, "E32.1.0.7", {"center": v(21.34, 49.02) * mm, "radius": 0.64 * mm});
            skCircle(sketch, "E32.1.0.8", {"center": v(42.67, 49.02) * mm, "radius": 0.64 * mm});
            skCircle(sketch, "E32.1.0.9", {"center": v(-7.11, 49.02) * mm, "radius": 0.64 * mm});
            skCircle(sketch, "E32.1.0.10", {"center": v(-3.56, 49.02) * mm, "radius": 0.64 * mm});
            skCircle(sketch, "E32.1.0.11", {"center": v(-10.67, 49.02) * mm, "radius": 0.64 * mm});
            skCircle(sketch, "E32.1.0.12", {"center": v(-14.22, 49.02) * mm, "radius": 0.64 * mm});
            skCircle(sketch, "E32.1.0.13", {"center": v(-21.34, 49.02) * mm, "radius": 0.64 * mm});
            skCircle(sketch, "E32.1.0.14", {"center": v(-24.9, 49.02) * mm, "radius": 0.64 * mm});
            skCircle(sketch, "E32.1.0.15", {"center": v(-28.45, 49.02) * mm, "radius": 0.64 * mm});
            skCircle(sketch, "E32.1.0.16", {"center": v(28.45, 49.02) * mm, "radius": 0.64 * mm});
            skCircle(sketch, "E32.1.0.17", {"center": v(7.11, 49.02) * mm, "radius": 0.64 * mm});
            skCircle(sketch, "E32.1.0.18", {"center": v(32, 49.02) * mm, "radius": 0.64 * mm});
            skCircle(sketch, "E32.1.0.19", {"center": v(35.56, 49.02) * mm, "radius": 0.64 * mm});
            skCircle(sketch, "E32.1.0.20", {"center": v(-17.78, 49.02) * mm, "radius": 0.64 * mm});
            skCircle(sketch, "E32.1.0.21", {"center": v(0, 49.02) * mm, "radius": 0.64 * mm});
            skCircle(sketch, "E32.1.0.22", {"center": v(24.9, 49.02) * mm, "radius": 0.64 * mm});
            skCircle(sketch, "E32.1.0.23", {"center": v(-42.67, 49.02) * mm, "radius": 0.64 * mm});
            skLineSegment(sketch, "E32.1.0.24", {"start": v(-42.67, 49.02) * mm, "end": v(-39.12, 49.02) * mm, "construction": true});
            skCircle(sketch, "E32.1.0.25", {"center": v(-39.12, 49.02) * mm, "radius": 0.64 * mm});
            skCircle(sketch, "E32.2.0.0", {"center": v(39.12, 45.36) * mm, "radius": 0.64 * mm});
            skCircle(sketch, "E32.2.0.1", {"center": v(14.22, 45.36) * mm, "radius": 0.64 * mm});
            skCircle(sketch, "E32.2.0.2", {"center": v(-32, 45.36) * mm, "radius": 0.64 * mm});
            skCircle(sketch, "E32.2.0.3", {"center": v(10.67, 45.36) * mm, "radius": 0.64 * mm});
            skCircle(sketch, "E32.2.0.4", {"center": v(-35.56, 45.36) * mm, "radius": 0.64 * mm});
            skCircle(sketch, "E32.2.0.5", {"center": v(17.78, 45.36) * mm, "radius": 0.64 * mm});
            skCircle(sketch, "E32.2.0.6", {"center": v(3.56, 45.36) * mm, "radius": 0.64 * mm});
            skCircle(sketch, "E32.2.0.7", {"center": v(21.34, 45.36) * mm, "radius": 0.64 * mm});
            skCircle(sketch, "E32.2.0.8", {"center": v(42.67, 45.36) * mm, "radius": 0.64 * mm});
            skCircle(sketch, "E32.2.0.9", {"center": v(-7.11, 45.36) * mm, "radius": 0.64 * mm});
            skCircle(sketch, "E32.2.0.10", {"center": v(-3.56, 45.36) * mm, "radius": 0.64 * mm});
            skCircle(sketch, "E32.2.0.11", {"center": v(-10.67, 45.36) * mm, "radius": 0.64 * mm});
            skCircle(sketch, "E32.2.0.12", {"center": v(-14.22, 45.36) * mm, "radius": 0.64 * mm});
            skCircle(sketch, "E32.2.0.13", {"center": v(-21.34, 45.36) * mm, "radius": 0.64 * mm});
            skCircle(sketch, "E32.2.0.14", {"center": v(-24.9, 45.36) * mm, "radius": 0.64 * mm});
            skCircle(sketch, "E32.2.0.15", {"center": v(-28.45, 45.36) * mm, "radius": 0.64 * mm});
            skCircle(sketch, "E32.2.0.16", {"center": v(28.45, 45.36) * mm, "radius": 0.64 * mm});
            skCircle(sketch, "E32.2.0.17", {"center": v(7.11, 45.36) * mm, "radius": 0.64 * mm});
            skCircle(sketch, "E32.2.0.18", {"center": v(32, 45.36) * mm, "radius": 0.64 * mm});
            skCircle(sketch, "E32.2.0.19", {"center": v(35.56, 45.36) * mm, "radius": 0.64 * mm});
            skCircle(sketch, "E32.2.0.20", {"center": v(-17.78, 45.36) * mm, "radius": 0.64 * mm});
            skCircle(sketch, "E32.2.0.21", {"center": v(0, 45.36) * mm, "radius": 0.64 * mm});
            skCircle(sketch, "E32.2.0.22", {"center": v(24.9, 45.36) * mm, "radius": 0.64 * mm});
            skCircle(sketch, "E32.2.0.23", {"center": v(-42.67, 45.36) * mm, "radius": 0.64 * mm});
            skLineSegment(sketch, "E32.2.0.24", {"start": v(-42.67, 45.36) * mm, "end": v(-39.12, 45.36) * mm, "construction": true});
            skCircle(sketch, "E32.2.0.25", {"center": v(-39.12, 45.36) * mm, "radius": 0.64 * mm});
            skCircle(sketch, "E32.3.0.0", {"center": v(39.12, 41.7) * mm, "radius": 0.64 * mm});
            skCircle(sketch, "E32.3.0.1", {"center": v(14.22, 41.7) * mm, "radius": 0.64 * mm});
            skCircle(sketch, "E32.3.0.2", {"center": v(-32, 41.7) * mm, "radius": 0.64 * mm});
            skCircle(sketch, "E32.3.0.3", {"center": v(10.67, 41.7) * mm, "radius": 0.64 * mm});
            skCircle(sketch, "E32.3.0.4", {"center": v(-35.56, 41.7) * mm, "radius": 0.64 * mm});
            skCircle(sketch, "E32.3.0.5", {"center": v(17.78, 41.7) * mm, "radius": 0.64 * mm});
            skCircle(sketch, "E32.3.0.6", {"center": v(3.56, 41.7) * mm, "radius": 0.64 * mm});
            skCircle(sketch, "E32.3.0.7", {"center": v(21.34, 41.7) * mm, "radius": 0.64 * mm});
            skCircle(sketch, "E32.3.0.8", {"center": v(42.67, 41.7) * mm, "radius": 0.64 * mm});
            skCircle(sketch, "E32.3.0.9", {"center": v(-7.11, 41.7) * mm, "radius": 0.64 * mm});
            skCircle(sketch, "E32.3.0.10", {"center": v(-3.56, 41.7) * mm, "radius": 0.64 * mm});
            skCircle(sketch, "E32.3.0.11", {"center": v(-10.67, 41.7) * mm, "radius": 0.64 * mm});
            skCircle(sketch, "E32.3.0.12", {"center": v(-14.22, 41.7) * mm, "radius": 0.64 * mm});
            skCircle(sketch, "E32.3.0.13", {"center": v(-21.34, 41.7) * mm, "radius": 0.64 * mm});
            skCircle(sketch, "E32.3.0.14", {"center": v(-24.9, 41.7) * mm, "radius": 0.64 * mm});
            skCircle(sketch, "E32.3.0.15", {"center": v(-28.45, 41.7) * mm, "radius": 0.64 * mm});
            skCircle(sketch, "E32.3.0.16", {"center": v(28.45, 41.7) * mm, "radius": 0.64 * mm});
            skCircle(sketch, "E32.3.0.17", {"center": v(7.11, 41.7) * mm, "radius": 0.64 * mm});
            skCircle(sketch, "E32.3.0.18", {"center": v(32, 41.7) * mm, "radius": 0.64 * mm});
            skCircle(sketch, "E32.3.0.19", {"center": v(35.56, 41.7) * mm, "radius": 0.64 * mm});
            skCircle(sketch, "E32.3.0.20", {"center": v(-17.78, 41.7) * mm, "radius": 0.64 * mm});
            skCircle(sketch, "E32.3.0.21", {"center": v(0, 41.7) * mm, "radius": 0.64 * mm});
            skCircle(sketch, "E32.3.0.22", {"center": v(24.9, 41.7) * mm, "radius": 0.64 * mm});
            skCircle(sketch, "E32.3.0.23", {"center": v(-42.67, 41.7) * mm, "radius": 0.64 * mm});
            skLineSegment(sketch, "E32.3.0.24", {"start": v(-42.67, 41.7) * mm, "end": v(-39.12, 41.7) * mm, "construction": true});
            skCircle(sketch, "E32.3.0.25", {"center": v(-39.12, 41.7) * mm, "radius": 0.64 * mm});
            skCircle(sketch, "E32.4.0.0", {"center": v(39.12, 38.05) * mm, "radius": 0.64 * mm});
            skCircle(sketch, "E32.4.0.1", {"center": v(14.22, 38.05) * mm, "radius": 0.64 * mm});
            skCircle(sketch, "E32.4.0.2", {"center": v(-32, 38.05) * mm, "radius": 0.64 * mm});
            skCircle(sketch, "E32.4.0.3", {"center": v(10.67, 38.05) * mm, "radius": 0.64 * mm});
            skCircle(sketch, "E32.4.0.4", {"center": v(-35.56, 38.05) * mm, "radius": 0.64 * mm});
            skCircle(sketch, "E32.4.0.5", {"center": v(17.78, 38.05) * mm, "radius": 0.64 * mm});
            skCircle(sketch, "E32.4.0.6", {"center": v(3.56, 38.05) * mm, "radius": 0.64 * mm});
            skCircle(sketch, "E32.4.0.7", {"center": v(21.34, 38.05) * mm, "radius": 0.64 * mm});
            skCircle(sketch, "E32.4.0.8", {"center": v(42.67, 38.05) * mm, "radius": 0.64 * mm});
            skCircle(sketch, "E32.4.0.9", {"center": v(-7.11, 38.05) * mm, "radius": 0.64 * mm});
            skCircle(sketch, "E32.4.0.10", {"center": v(-3.56, 38.05) * mm, "radius": 0.64 * mm});
            skCircle(sketch, "E32.4.0.11", {"center": v(-10.67, 38.05) * mm, "radius": 0.64 * mm});
            skCircle(sketch, "E32.4.0.12", {"center": v(-14.22, 38.05) * mm, "radius": 0.64 * mm});
            skCircle(sketch, "E32.4.0.13", {"center": v(-21.34, 38.05) * mm, "radius": 0.64 * mm});
            skCircle(sketch, "E32.4.0.14", {"center": v(-24.9, 38.05) * mm, "radius": 0.64 * mm});
            skCircle(sketch, "E32.4.0.15", {"center": v(-28.45, 38.05) * mm, "radius": 0.64 * mm});
            skCircle(sketch, "E32.4.0.16", {"center": v(28.45, 38.05) * mm, "radius": 0.64 * mm});
            skCircle(sketch, "E32.4.0.17", {"center": v(7.11, 38.05) * mm, "radius": 0.64 * mm});
            skCircle(sketch, "E32.4.0.18", {"center": v(32, 38.05) * mm, "radius": 0.64 * mm});
            skCircle(sketch, "E32.4.0.19", {"center": v(35.56, 38.05) * mm, "radius": 0.64 * mm});
            skCircle(sketch, "E32.4.0.20", {"center": v(-17.78, 38.05) * mm, "radius": 0.64 * mm});
            skCircle(sketch, "E32.4.0.21", {"center": v(0, 38.05) * mm, "radius": 0.64 * mm});
            skCircle(sketch, "E32.4.0.22", {"center": v(24.9, 38.05) * mm, "radius": 0.64 * mm});
            skCircle(sketch, "E32.4.0.23", {"center": v(-42.67, 38.05) * mm, "radius": 0.64 * mm});
            skLineSegment(sketch, "E32.4.0.24", {"start": v(-42.67, 38.05) * mm, "end": v(-39.12, 38.05) * mm, "construction": true});
            skCircle(sketch, "E32.4.0.25", {"center": v(-39.12, 38.05) * mm, "radius": 0.64 * mm});
            skCircle(sketch, "E32.5.0.0", {"center": v(39.12, 34.4) * mm, "radius": 0.64 * mm});
            skCircle(sketch, "E32.5.0.1", {"center": v(14.22, 34.4) * mm, "radius": 0.64 * mm});
            skCircle(sketch, "E32.5.0.2", {"center": v(-32, 34.4) * mm, "radius": 0.64 * mm});
            skCircle(sketch, "E32.5.0.3", {"center": v(10.67, 34.4) * mm, "radius": 0.64 * mm});
            skCircle(sketch, "E32.5.0.4", {"center": v(-35.56, 34.4) * mm, "radius": 0.64 * mm});
            skCircle(sketch, "E32.5.0.5", {"center": v(17.78, 34.4) * mm, "radius": 0.64 * mm});
            skCircle(sketch, "E32.5.0.6", {"center": v(3.56, 34.4) * mm, "radius": 0.64 * mm});
            skCircle(sketch, "E32.5.0.7", {"center": v(21.34, 34.4) * mm, "radius": 0.64 * mm});
            skCircle(sketch, "E32.5.0.8", {"center": v(42.67, 34.4) * mm, "radius": 0.64 * mm});
            skCircle(sketch, "E32.5.0.9", {"center": v(-7.11, 34.4) * mm, "radius": 0.64 * mm});
            skCircle(sketch, "E32.5.0.10", {"center": v(-3.56, 34.4) * mm, "radius": 0.64 * mm});
            skCircle(sketch, "E32.5.0.11", {"center": v(-10.67, 34.4) * mm, "radius": 0.64 * mm});
            skCircle(sketch, "E32.5.0.12", {"center": v(-14.22, 34.4) * mm, "radius": 0.64 * mm});
            skCircle(sketch, "E32.5.0.13", {"center": v(-21.34, 34.4) * mm, "radius": 0.64 * mm});
            skCircle(sketch, "E32.5.0.14", {"center": v(-24.9, 34.4) * mm, "radius": 0.64 * mm});
            skCircle(sketch, "E32.5.0.15", {"center": v(-28.45, 34.4) * mm, "radius": 0.64 * mm});
            skCircle(sketch, "E32.5.0.16", {"center": v(28.45, 34.4) * mm, "radius": 0.64 * mm});
            skCircle(sketch, "E32.5.0.17", {"center": v(7.11, 34.4) * mm, "radius": 0.64 * mm});
            skCircle(sketch, "E32.5.0.18", {"center": v(32, 34.4) * mm, "radius": 0.64 * mm});
            skCircle(sketch, "E32.5.0.19", {"center": v(35.56, 34.4) * mm, "radius": 0.64 * mm});
            skCircle(sketch, "E32.5.0.20", {"center": v(-17.78, 34.4) * mm, "radius": 0.64 * mm});
            skCircle(sketch, "E32.5.0.21", {"center": v(0, 34.4) * mm, "radius": 0.64 * mm});
            skCircle(sketch, "E32.5.0.22", {"center": v(24.9, 34.4) * mm, "radius": 0.64 * mm});
            skCircle(sketch, "E32.5.0.23", {"center": v(-42.67, 34.4) * mm, "radius": 0.64 * mm});
            skLineSegment(sketch, "E32.5.0.24", {"start": v(-42.67, 34.4) * mm, "end": v(-39.12, 34.4) * mm, "construction": true});
            skCircle(sketch, "E32.5.0.25", {"center": v(-39.12, 34.4) * mm, "radius": 0.64 * mm});
            skCircle(sketch, "E32.6.0.0", {"center": v(39.12, 30.73) * mm, "radius": 0.64 * mm});
            skCircle(sketch, "E32.6.0.1", {"center": v(14.22, 30.73) * mm, "radius": 0.64 * mm});
            skCircle(sketch, "E32.6.0.2", {"center": v(-32, 30.73) * mm, "radius": 0.64 * mm});
            skCircle(sketch, "E32.6.0.3", {"center": v(10.67, 30.73) * mm, "radius": 0.64 * mm});
            skCircle(sketch, "E32.6.0.4", {"center": v(-35.56, 30.73) * mm, "radius": 0.64 * mm});
            skCircle(sketch, "E32.6.0.5", {"center": v(17.78, 30.73) * mm, "radius": 0.64 * mm});
            skCircle(sketch, "E32.6.0.6", {"center": v(3.56, 30.73) * mm, "radius": 0.64 * mm});
            skCircle(sketch, "E32.6.0.7", {"center": v(21.34, 30.73) * mm, "radius": 0.64 * mm});
            skCircle(sketch, "E32.6.0.8", {"center": v(42.67, 30.73) * mm, "radius": 0.64 * mm});
            skCircle(sketch, "E32.6.0.9", {"center": v(-7.11, 30.73) * mm, "radius": 0.64 * mm});
            skCircle(sketch, "E32.6.0.10", {"center": v(-3.56, 30.73) * mm, "radius": 0.64 * mm});
            skCircle(sketch, "E32.6.0.11", {"center": v(-10.67, 30.73) * mm, "radius": 0.64 * mm});
            skCircle(sketch, "E32.6.0.12", {"center": v(-14.22, 30.73) * mm, "radius": 0.64 * mm});
            skCircle(sketch, "E32.6.0.13", {"center": v(-21.34, 30.73) * mm, "radius": 0.64 * mm});
            skCircle(sketch, "E32.6.0.14", {"center": v(-24.9, 30.73) * mm, "radius": 0.64 * mm});
            skCircle(sketch, "E32.6.0.15", {"center": v(-28.45, 30.73) * mm, "radius": 0.64 * mm});
            skCircle(sketch, "E32.6.0.16", {"center": v(28.45, 30.73) * mm, "radius": 0.64 * mm});
            skCircle(sketch, "E32.6.0.17", {"center": v(7.11, 30.73) * mm, "radius": 0.64 * mm});
            skCircle(sketch, "E32.6.0.18", {"center": v(32, 30.73) * mm, "radius": 0.64 * mm});
            skCircle(sketch, "E32.6.0.19", {"center": v(35.56, 30.73) * mm, "radius": 0.64 * mm});
            skCircle(sketch, "E32.6.0.20", {"center": v(-17.78, 30.73) * mm, "radius": 0.64 * mm});
            skCircle(sketch, "E32.6.0.21", {"center": v(0, 30.73) * mm, "radius": 0.64 * mm});
            skCircle(sketch, "E32.6.0.22", {"center": v(24.9, 30.73) * mm, "radius": 0.64 * mm});
            skCircle(sketch, "E32.6.0.23", {"center": v(-42.67, 30.73) * mm, "radius": 0.64 * mm});
            skLineSegment(sketch, "E32.6.0.24", {"start": v(-42.67, 30.73) * mm, "end": v(-39.12, 30.73) * mm, "construction": true});
            skCircle(sketch, "E32.6.0.25", {"center": v(-39.12, 30.73) * mm, "radius": 0.64 * mm});
            skCircle(sketch, "E32.7.0.0", {"center": v(39.12, 27.08) * mm, "radius": 0.64 * mm});
            skCircle(sketch, "E32.7.0.1", {"center": v(14.22, 27.08) * mm, "radius": 0.64 * mm});
            skCircle(sketch, "E32.7.0.2", {"center": v(-32, 27.08) * mm, "radius": 0.64 * mm});
            skCircle(sketch, "E32.7.0.3", {"center": v(10.67, 27.08) * mm, "radius": 0.64 * mm});
            skCircle(sketch, "E32.7.0.4", {"center": v(-35.56, 27.08) * mm, "radius": 0.64 * mm});
            skCircle(sketch, "E32.7.0.5", {"center": v(17.78, 27.08) * mm, "radius": 0.64 * mm});
            skCircle(sketch, "E32.7.0.6", {"center": v(3.56, 27.08) * mm, "radius": 0.64 * mm});
            skCircle(sketch, "E32.7.0.7", {"center": v(21.34, 27.08) * mm, "radius": 0.64 * mm});
            skCircle(sketch, "E32.7.0.8", {"center": v(42.67, 27.08) * mm, "radius": 0.64 * mm});
            skCircle(sketch, "E32.7.0.9", {"center": v(-7.11, 27.08) * mm, "radius": 0.64 * mm});
            skCircle(sketch, "E32.7.0.10", {"center": v(-3.56, 27.08) * mm, "radius": 0.64 * mm});
            skCircle(sketch, "E32.7.0.11", {"center": v(-10.67, 27.08) * mm, "radius": 0.64 * mm});
            skCircle(sketch, "E32.7.0.12", {"center": v(-14.22, 27.08) * mm, "radius": 0.64 * mm});
            skCircle(sketch, "E32.7.0.13", {"center": v(-21.34, 27.08) * mm, "radius": 0.64 * mm});
            skCircle(sketch, "E32.7.0.14", {"center": v(-24.9, 27.08) * mm, "radius": 0.64 * mm});
            skCircle(sketch, "E32.7.0.15", {"center": v(-28.45, 27.08) * mm, "radius": 0.64 * mm});
            skCircle(sketch, "E32.7.0.16", {"center": v(28.45, 27.08) * mm, "radius": 0.64 * mm});
            skCircle(sketch, "E32.7.0.17", {"center": v(7.11, 27.08) * mm, "radius": 0.64 * mm});
            skCircle(sketch, "E32.7.0.18", {"center": v(32, 27.08) * mm, "radius": 0.64 * mm});
            skCircle(sketch, "E32.7.0.19", {"center": v(35.56, 27.08) * mm, "radius": 0.64 * mm});
            skCircle(sketch, "E32.7.0.20", {"center": v(-17.78, 27.08) * mm, "radius": 0.64 * mm});
            skCircle(sketch, "E32.7.0.21", {"center": v(0, 27.08) * mm, "radius": 0.64 * mm});
            skCircle(sketch, "E32.7.0.22", {"center": v(24.9, 27.08) * mm, "radius": 0.64 * mm});
            skCircle(sketch, "E32.7.0.23", {"center": v(-42.67, 27.08) * mm, "radius": 0.64 * mm});
            skLineSegment(sketch, "E32.7.0.24", {"start": v(-42.67, 27.08) * mm, "end": v(-39.12, 27.08) * mm, "construction": true});
            skCircle(sketch, "E32.7.0.25", {"center": v(-39.12, 27.08) * mm, "radius": 0.64 * mm});
            skCircle(sketch, "E32.8.0.0", {"center": v(39.12, 23.42) * mm, "radius": 0.64 * mm});
            skCircle(sketch, "E32.8.0.1", {"center": v(14.22, 23.42) * mm, "radius": 0.64 * mm});
            skCircle(sketch, "E32.8.0.2", {"center": v(-32, 23.42) * mm, "radius": 0.64 * mm});
            skCircle(sketch, "E32.8.0.3", {"center": v(10.67, 23.42) * mm, "radius": 0.64 * mm});
            skCircle(sketch, "E32.8.0.4", {"center": v(-35.56, 23.42) * mm, "radius": 0.64 * mm});
            skCircle(sketch, "E32.8.0.5", {"center": v(17.78, 23.42) * mm, "radius": 0.64 * mm});
            skCircle(sketch, "E32.8.0.6", {"center": v(3.56, 23.42) * mm, "radius": 0.64 * mm});
            skCircle(sketch, "E32.8.0.7", {"center": v(21.34, 23.42) * mm, "radius": 0.64 * mm});
            skCircle(sketch, "E32.8.0.8", {"center": v(42.67, 23.42) * mm, "radius": 0.64 * mm});
            skCircle(sketch, "E32.8.0.9", {"center": v(-7.11, 23.42) * mm, "radius": 0.64 * mm});
            skCircle(sketch, "E32.8.0.10", {"center": v(-3.56, 23.42) * mm, "radius": 0.64 * mm});
            skCircle(sketch, "E32.8.0.11", {"center": v(-10.67, 23.42) * mm, "radius": 0.64 * mm});
            skCircle(sketch, "E32.8.0.12", {"center": v(-14.22, 23.42) * mm, "radius": 0.64 * mm});
            skCircle(sketch, "E32.8.0.13", {"center": v(-21.34, 23.42) * mm, "radius": 0.64 * mm});
            skCircle(sketch, "E32.8.0.14", {"center": v(-24.9, 23.42) * mm, "radius": 0.64 * mm});
            skCircle(sketch, "E32.8.0.15", {"center": v(-28.45, 23.42) * mm, "radius": 0.64 * mm});
            skCircle(sketch, "E32.8.0.16", {"center": v(28.45, 23.42) * mm, "radius": 0.64 * mm});
            skCircle(sketch, "E32.8.0.17", {"center": v(7.11, 23.42) * mm, "radius": 0.64 * mm});
            skCircle(sketch, "E32.8.0.18", {"center": v(32, 23.42) * mm, "radius": 0.64 * mm});
            skCircle(sketch, "E32.8.0.19", {"center": v(35.56, 23.42) * mm, "radius": 0.64 * mm});
            skCircle(sketch, "E32.8.0.20", {"center": v(-17.78, 23.42) * mm, "radius": 0.64 * mm});
            skCircle(sketch, "E32.8.0.21", {"center": v(0, 23.42) * mm, "radius": 0.64 * mm});
            skCircle(sketch, "E32.8.0.22", {"center": v(24.9, 23.42) * mm, "radius": 0.64 * mm});
            skCircle(sketch, "E32.8.0.23", {"center": v(-42.67, 23.42) * mm, "radius": 0.64 * mm});
            skLineSegment(sketch, "E32.8.0.24", {"start": v(-42.67, 23.42) * mm, "end": v(-39.12, 23.42) * mm, "construction": true});
            skCircle(sketch, "E32.8.0.25", {"center": v(-39.12, 23.42) * mm, "radius": 0.64 * mm});
            skCircle(sketch, "E32.9.0.0", {"center": v(39.12, 19.76) * mm, "radius": 0.64 * mm});
            skCircle(sketch, "E32.9.0.1", {"center": v(14.22, 19.76) * mm, "radius": 0.64 * mm});
            skCircle(sketch, "E32.9.0.2", {"center": v(-32, 19.76) * mm, "radius": 0.64 * mm});
            skCircle(sketch, "E32.9.0.3", {"center": v(10.67, 19.76) * mm, "radius": 0.64 * mm});
            skCircle(sketch, "E32.9.0.4", {"center": v(-35.56, 19.76) * mm, "radius": 0.64 * mm});
            skCircle(sketch, "E32.9.0.5", {"center": v(17.78, 19.76) * mm, "radius": 0.64 * mm});
            skCircle(sketch, "E32.9.0.6", {"center": v(3.56, 19.76) * mm, "radius": 0.64 * mm});
            skCircle(sketch, "E32.9.0.7", {"center": v(21.34, 19.76) * mm, "radius": 0.64 * mm});
            skCircle(sketch, "E32.9.0.8", {"center": v(42.67, 19.76) * mm, "radius": 0.64 * mm});
            skCircle(sketch, "E32.9.0.9", {"center": v(-7.11, 19.76) * mm, "radius": 0.64 * mm});
            skCircle(sketch, "E32.9.0.10", {"center": v(-3.56, 19.76) * mm, "radius": 0.64 * mm});
            skCircle(sketch, "E32.9.0.11", {"center": v(-10.67, 19.76) * mm, "radius": 0.64 * mm});
            skCircle(sketch, "E32.9.0.12", {"center": v(-14.22, 19.76) * mm, "radius": 0.64 * mm});
            skCircle(sketch, "E32.9.0.13", {"center": v(-21.34, 19.76) * mm, "radius": 0.64 * mm});
            skCircle(sketch, "E32.9.0.14", {"center": v(-24.9, 19.76) * mm, "radius": 0.64 * mm});
            skCircle(sketch, "E32.9.0.15", {"center": v(-28.45, 19.76) * mm, "radius": 0.64 * mm});
            skCircle(sketch, "E32.9.0.16", {"center": v(28.45, 19.76) * mm, "radius": 0.64 * mm});
            skCircle(sketch, "E32.9.0.17", {"center": v(7.11, 19.76) * mm, "radius": 0.64 * mm});
            skCircle(sketch, "E32.9.0.18", {"center": v(32, 19.76) * mm, "radius": 0.64 * mm});
            skCircle(sketch, "E32.9.0.19", {"center": v(35.56, 19.76) * mm, "radius": 0.64 * mm});
            skCircle(sketch, "E32.9.0.20", {"center": v(-17.78, 19.76) * mm, "radius": 0.64 * mm});
            skCircle(sketch, "E32.9.0.21", {"center": v(0, 19.76) * mm, "radius": 0.64 * mm});
            skCircle(sketch, "E32.9.0.22", {"center": v(24.9, 19.76) * mm, "radius": 0.64 * mm});
            skCircle(sketch, "E32.9.0.23", {"center": v(-42.67, 19.76) * mm, "radius": 0.64 * mm});
            skLineSegment(sketch, "E32.9.0.24", {"start": v(-42.67, 19.76) * mm, "end": v(-39.12, 19.76) * mm, "construction": true});
            skCircle(sketch, "E32.9.0.25", {"center": v(-39.12, 19.76) * mm, "radius": 0.64 * mm});
            skCircle(sketch, "E32.10.0.0", {"center": v(39.12, 16.1) * mm, "radius": 0.64 * mm});
            skCircle(sketch, "E32.10.0.1", {"center": v(14.22, 16.1) * mm, "radius": 0.64 * mm});
            skCircle(sketch, "E32.10.0.2", {"center": v(-32, 16.1) * mm, "radius": 0.64 * mm});
            skCircle(sketch, "E32.10.0.3", {"center": v(10.67, 16.1) * mm, "radius": 0.64 * mm});
            skCircle(sketch, "E32.10.0.4", {"center": v(-35.56, 16.1) * mm, "radius": 0.64 * mm});
            skCircle(sketch, "E32.10.0.5", {"center": v(17.78, 16.1) * mm, "radius": 0.64 * mm});
            skCircle(sketch, "E32.10.0.6", {"center": v(3.56, 16.1) * mm, "radius": 0.64 * mm});
            skCircle(sketch, "E32.10.0.7", {"center": v(21.34, 16.1) * mm, "radius": 0.64 * mm});
            skCircle(sketch, "E32.10.0.8", {"center": v(42.67, 16.1) * mm, "radius": 0.64 * mm});
            skCircle(sketch, "E32.10.0.9", {"center": v(-7.11, 16.1) * mm, "radius": 0.64 * mm});
            skCircle(sketch, "E32.10.0.10", {"center": v(-3.56, 16.1) * mm, "radius": 0.64 * mm});
            skCircle(sketch, "E32.10.0.11", {"center": v(-10.67, 16.1) * mm, "radius": 0.64 * mm});
            skCircle(sketch, "E32.10.0.12", {"center": v(-14.22, 16.1) * mm, "radius": 0.64 * mm});
            skCircle(sketch, "E32.10.0.13", {"center": v(-21.34, 16.1) * mm, "radius": 0.64 * mm});
            skCircle(sketch, "E32.10.0.14", {"center": v(-24.9, 16.1) * mm, "radius": 0.64 * mm});
            skCircle(sketch, "E32.10.0.15", {"center": v(-28.45, 16.1) * mm, "radius": 0.64 * mm});
            skCircle(sketch, "E32.10.0.16", {"center": v(28.45, 16.1) * mm, "radius": 0.64 * mm});
            skCircle(sketch, "E32.10.0.17", {"center": v(7.11, 16.1) * mm, "radius": 0.64 * mm});
            skCircle(sketch, "E32.10.0.18", {"center": v(32, 16.1) * mm, "radius": 0.64 * mm});
            skCircle(sketch, "E32.10.0.19", {"center": v(35.56, 16.1) * mm, "radius": 0.64 * mm});
            skCircle(sketch, "E32.10.0.20", {"center": v(-17.78, 16.1) * mm, "radius": 0.64 * mm});
            skCircle(sketch, "E32.10.0.21", {"center": v(0, 16.1) * mm, "radius": 0.64 * mm});
            skCircle(sketch, "E32.10.0.22", {"center": v(24.9, 16.1) * mm, "radius": 0.64 * mm});
            skCircle(sketch, "E32.10.0.23", {"center": v(-42.67, 16.1) * mm, "radius": 0.64 * mm});
            skLineSegment(sketch, "E32.10.0.24", {"start": v(-42.67, 16.1) * mm, "end": v(-39.12, 16.1) * mm, "construction": true});
            skCircle(sketch, "E32.10.0.25", {"center": v(-39.12, 16.1) * mm, "radius": 0.64 * mm});
            skCircle(sketch, "E32.11.0.0", {"center": v(39.12, 12.45) * mm, "radius": 0.64 * mm});
            skCircle(sketch, "E32.11.0.1", {"center": v(14.22, 12.45) * mm, "radius": 0.64 * mm});
            skCircle(sketch, "E32.11.0.2", {"center": v(-32, 12.45) * mm, "radius": 0.64 * mm});
            skCircle(sketch, "E32.11.0.3", {"center": v(10.67, 12.45) * mm, "radius": 0.64 * mm});
            skCircle(sketch, "E32.11.0.4", {"center": v(-35.56, 12.45) * mm, "radius": 0.64 * mm});
            skCircle(sketch, "E32.11.0.5", {"center": v(17.78, 12.45) * mm, "radius": 0.64 * mm});
            skCircle(sketch, "E32.11.0.6", {"center": v(3.56, 12.45) * mm, "radius": 0.64 * mm});
            skCircle(sketch, "E32.11.0.7", {"center": v(21.34, 12.45) * mm, "radius": 0.64 * mm});
            skCircle(sketch, "E32.11.0.8", {"center": v(42.67, 12.45) * mm, "radius": 0.64 * mm});
            skCircle(sketch, "E32.11.0.9", {"center": v(-7.11, 12.45) * mm, "radius": 0.64 * mm});
            skCircle(sketch, "E32.11.0.10", {"center": v(-3.56, 12.45) * mm, "radius": 0.64 * mm});
            skCircle(sketch, "E32.11.0.11", {"center": v(-10.67, 12.45) * mm, "radius": 0.64 * mm});
            skCircle(sketch, "E32.11.0.12", {"center": v(-14.22, 12.45) * mm, "radius": 0.64 * mm});
            skCircle(sketch, "E32.11.0.13", {"center": v(-21.34, 12.45) * mm, "radius": 0.64 * mm});
            skCircle(sketch, "E32.11.0.14", {"center": v(-24.9, 12.45) * mm, "radius": 0.64 * mm});
            skCircle(sketch, "E32.11.0.15", {"center": v(-28.45, 12.45) * mm, "radius": 0.64 * mm});
            skCircle(sketch, "E32.11.0.16", {"center": v(28.45, 12.45) * mm, "radius": 0.64 * mm});
            skCircle(sketch, "E32.11.0.17", {"center": v(7.11, 12.45) * mm, "radius": 0.64 * mm});
            skCircle(sketch, "E32.11.0.18", {"center": v(32, 12.45) * mm, "radius": 0.64 * mm});
            skCircle(sketch, "E32.11.0.19", {"center": v(35.56, 12.45) * mm, "radius": 0.64 * mm});
            skCircle(sketch, "E32.11.0.20", {"center": v(-17.78, 12.45) * mm, "radius": 0.64 * mm});
            skCircle(sketch, "E32.11.0.21", {"center": v(0, 12.45) * mm, "radius": 0.64 * mm});
            skCircle(sketch, "E32.11.0.22", {"center": v(24.9, 12.45) * mm, "radius": 0.64 * mm});
            skCircle(sketch, "E32.11.0.23", {"center": v(-42.67, 12.45) * mm, "radius": 0.64 * mm});
            skLineSegment(sketch, "E32.11.0.24", {"start": v(-42.67, 12.45) * mm, "end": v(-39.12, 12.45) * mm, "construction": true});
            skCircle(sketch, "E32.11.0.25", {"center": v(-39.12, 12.45) * mm, "radius": 0.64 * mm});
            skCircle(sketch, "E32.12.0.0", {"center": v(39.12, 8.79) * mm, "radius": 0.64 * mm});
            skCircle(sketch, "E32.12.0.1", {"center": v(14.22, 8.79) * mm, "radius": 0.64 * mm});
            skCircle(sketch, "E32.12.0.2", {"center": v(-32, 8.79) * mm, "radius": 0.64 * mm});
            skCircle(sketch, "E32.12.0.3", {"center": v(10.67, 8.79) * mm, "radius": 0.64 * mm});
            skCircle(sketch, "E32.12.0.4", {"center": v(-35.56, 8.79) * mm, "radius": 0.64 * mm});
            skCircle(sketch, "E32.12.0.5", {"center": v(17.78, 8.79) * mm, "radius": 0.64 * mm});
            skCircle(sketch, "E32.12.0.6", {"center": v(3.56, 8.79) * mm, "radius": 0.64 * mm});
            skCircle(sketch, "E32.12.0.7", {"center": v(21.34, 8.79) * mm, "radius": 0.64 * mm});
            skCircle(sketch, "E32.12.0.8", {"center": v(42.67, 8.79) * mm, "radius": 0.64 * mm});
            skCircle(sketch, "E32.12.0.9", {"center": v(-7.11, 8.79) * mm, "radius": 0.64 * mm});
            skCircle(sketch, "E32.12.0.10", {"center": v(-3.56, 8.79) * mm, "radius": 0.64 * mm});
            skCircle(sketch, "E32.12.0.11", {"center": v(-10.67, 8.79) * mm, "radius": 0.64 * mm});
            skCircle(sketch, "E32.12.0.12", {"center": v(-14.22, 8.79) * mm, "radius": 0.64 * mm});
            skCircle(sketch, "E32.12.0.13", {"center": v(-21.34, 8.79) * mm, "radius": 0.64 * mm});
            skCircle(sketch, "E32.12.0.14", {"center": v(-24.9, 8.79) * mm, "radius": 0.64 * mm});
            skCircle(sketch, "E32.12.0.15", {"center": v(-28.45, 8.79) * mm, "radius": 0.64 * mm});
            skCircle(sketch, "E32.12.0.16", {"center": v(28.45, 8.79) * mm, "radius": 0.64 * mm});
            skCircle(sketch, "E32.12.0.17", {"center": v(7.11, 8.79) * mm, "radius": 0.64 * mm});
            skCircle(sketch, "E32.12.0.18", {"center": v(32, 8.79) * mm, "radius": 0.64 * mm});
            skCircle(sketch, "E32.12.0.19", {"center": v(35.56, 8.79) * mm, "radius": 0.64 * mm});
            skCircle(sketch, "E32.12.0.20", {"center": v(-17.78, 8.79) * mm, "radius": 0.64 * mm});
            skCircle(sketch, "E32.12.0.21", {"center": v(0, 8.79) * mm, "radius": 0.64 * mm});
            skCircle(sketch, "E32.12.0.22", {"center": v(24.9, 8.79) * mm, "radius": 0.64 * mm});
            skCircle(sketch, "E32.12.0.23", {"center": v(-42.67, 8.79) * mm, "radius": 0.64 * mm});
            skLineSegment(sketch, "E32.12.0.24", {"start": v(-42.67, 8.79) * mm, "end": v(-39.12, 8.79) * mm, "construction": true});
            skCircle(sketch, "E32.12.0.25", {"center": v(-39.12, 8.79) * mm, "radius": 0.64 * mm});
            skCircle(sketch, "E32.13.0.0", {"center": v(39.12, 5.13) * mm, "radius": 0.64 * mm});
            skCircle(sketch, "E32.13.0.1", {"center": v(14.22, 5.13) * mm, "radius": 0.64 * mm});
            skCircle(sketch, "E32.13.0.2", {"center": v(-32, 5.13) * mm, "radius": 0.64 * mm});
            skCircle(sketch, "E32.13.0.3", {"center": v(10.67, 5.13) * mm, "radius": 0.64 * mm});
            skCircle(sketch, "E32.13.0.4", {"center": v(-35.56, 5.13) * mm, "radius": 0.64 * mm});
            skCircle(sketch, "E32.13.0.5", {"center": v(17.78, 5.13) * mm, "radius": 0.64 * mm});
            skCircle(sketch, "E32.13.0.6", {"center": v(3.56, 5.13) * mm, "radius": 0.64 * mm});
            skCircle(sketch, "E32.13.0.7", {"center": v(21.34, 5.13) * mm, "radius": 0.64 * mm});
            skCircle(sketch, "E32.13.0.8", {"center": v(42.67, 5.13) * mm, "radius": 0.64 * mm});
            skCircle(sketch, "E32.13.0.9", {"center": v(-7.11, 5.13) * mm, "radius": 0.64 * mm});
            skCircle(sketch, "E32.13.0.10", {"center": v(-3.56, 5.13) * mm, "radius": 0.64 * mm});
            skCircle(sketch, "E32.13.0.11", {"center": v(-10.67, 5.13) * mm, "radius": 0.64 * mm});
            skCircle(sketch, "E32.13.0.12", {"center": v(-14.22, 5.13) * mm, "radius": 0.64 * mm});
            skCircle(sketch, "E32.13.0.13", {"center": v(-21.34, 5.13) * mm, "radius": 0.64 * mm});
            skCircle(sketch, "E32.13.0.14", {"center": v(-24.9, 5.13) * mm, "radius": 0.64 * mm});
            skCircle(sketch, "E32.13.0.15", {"center": v(-28.45, 5.13) * mm, "radius": 0.64 * mm});
            skCircle(sketch, "E32.13.0.16", {"center": v(28.45, 5.13) * mm, "radius": 0.64 * mm});
            skCircle(sketch, "E32.13.0.17", {"center": v(7.11, 5.13) * mm, "radius": 0.64 * mm});
            skCircle(sketch, "E32.13.0.18", {"center": v(32, 5.13) * mm, "radius": 0.64 * mm});
            skCircle(sketch, "E32.13.0.19", {"center": v(35.56, 5.13) * mm, "radius": 0.64 * mm});
            skCircle(sketch, "E32.13.0.20", {"center": v(-17.78, 5.13) * mm, "radius": 0.64 * mm});
            skCircle(sketch, "E32.13.0.21", {"center": v(0, 5.13) * mm, "radius": 0.64 * mm});
            skCircle(sketch, "E32.13.0.22", {"center": v(24.9, 5.13) * mm, "radius": 0.64 * mm});
            skCircle(sketch, "E32.13.0.23", {"center": v(-42.67, 5.13) * mm, "radius": 0.64 * mm});
            skLineSegment(sketch, "E32.13.0.24", {"start": v(-42.67, 5.13) * mm, "end": v(-39.12, 5.13) * mm, "construction": true});
            skCircle(sketch, "E32.13.0.25", {"center": v(-39.12, 5.13) * mm, "radius": 0.64 * mm});
            skCircle(sketch, "E32.14.0.0", {"center": v(39.12, 1.47) * mm, "radius": 0.64 * mm});
            skCircle(sketch, "E32.14.0.1", {"center": v(14.22, 1.47) * mm, "radius": 0.64 * mm});
            skCircle(sketch, "E32.14.0.2", {"center": v(-32, 1.47) * mm, "radius": 0.64 * mm});
            skCircle(sketch, "E32.14.0.3", {"center": v(10.67, 1.47) * mm, "radius": 0.64 * mm});
            skCircle(sketch, "E32.14.0.4", {"center": v(-35.56, 1.47) * mm, "radius": 0.64 * mm});
            skCircle(sketch, "E32.14.0.5", {"center": v(17.78, 1.47) * mm, "radius": 0.64 * mm});
            skCircle(sketch, "E32.14.0.6", {"center": v(3.56, 1.47) * mm, "radius": 0.64 * mm});
            skCircle(sketch, "E32.14.0.7", {"center": v(21.34, 1.47) * mm, "radius": 0.64 * mm});
            skCircle(sketch, "E32.14.0.8", {"center": v(42.67, 1.47) * mm, "radius": 0.64 * mm});
            skCircle(sketch, "E32.14.0.9", {"center": v(-7.11, 1.47) * mm, "radius": 0.64 * mm});
            skCircle(sketch, "E32.14.0.10", {"center": v(-3.56, 1.47) * mm, "radius": 0.64 * mm});
            skCircle(sketch, "E32.14.0.11", {"center": v(-10.67, 1.47) * mm, "radius": 0.64 * mm});
            skCircle(sketch, "E32.14.0.12", {"center": v(-14.22, 1.47) * mm, "radius": 0.64 * mm});
            skCircle(sketch, "E32.14.0.13", {"center": v(-21.34, 1.47) * mm, "radius": 0.64 * mm});
            skCircle(sketch, "E32.14.0.14", {"center": v(-24.9, 1.47) * mm, "radius": 0.64 * mm});
            skCircle(sketch, "E32.14.0.15", {"center": v(-28.45, 1.47) * mm, "radius": 0.64 * mm});
            skCircle(sketch, "E32.14.0.16", {"center": v(28.45, 1.47) * mm, "radius": 0.64 * mm});
            skCircle(sketch, "E32.14.0.17", {"center": v(7.11, 1.47) * mm, "radius": 0.64 * mm});
            skCircle(sketch, "E32.14.0.18", {"center": v(32, 1.47) * mm, "radius": 0.64 * mm});
            skCircle(sketch, "E32.14.0.19", {"center": v(35.56, 1.47) * mm, "radius": 0.64 * mm});
            skCircle(sketch, "E32.14.0.20", {"center": v(-17.78, 1.47) * mm, "radius": 0.64 * mm});
            skCircle(sketch, "E32.14.0.21", {"center": v(0, 1.47) * mm, "radius": 0.64 * mm});
            skCircle(sketch, "E32.14.0.22", {"center": v(24.9, 1.47) * mm, "radius": 0.64 * mm});
            skCircle(sketch, "E32.14.0.23", {"center": v(-42.67, 1.47) * mm, "radius": 0.64 * mm});
            skLineSegment(sketch, "E32.14.0.24", {"start": v(-42.67, 1.47) * mm, "end": v(-39.12, 1.47) * mm, "construction": true});
            skCircle(sketch, "E32.14.0.25", {"center": v(-39.12, 1.47) * mm, "radius": 0.64 * mm});
            skCircle(sketch, "E32.15.0.0", {"center": v(39.12, -2.18) * mm, "radius": 0.64 * mm});
            skCircle(sketch, "E32.15.0.1", {"center": v(14.22, -2.18) * mm, "radius": 0.64 * mm});
            skCircle(sketch, "E32.15.0.2", {"center": v(-32, -2.18) * mm, "radius": 0.64 * mm});
            skCircle(sketch, "E32.15.0.3", {"center": v(10.67, -2.18) * mm, "radius": 0.64 * mm});
            skCircle(sketch, "E32.15.0.4", {"center": v(-35.56, -2.18) * mm, "radius": 0.64 * mm});
            skCircle(sketch, "E32.15.0.5", {"center": v(17.78, -2.18) * mm, "radius": 0.64 * mm});
            skCircle(sketch, "E32.15.0.6", {"center": v(3.56, -2.18) * mm, "radius": 0.64 * mm});
            skCircle(sketch, "E32.15.0.7", {"center": v(21.34, -2.18) * mm, "radius": 0.64 * mm});
            skCircle(sketch, "E32.15.0.8", {"center": v(42.67, -2.18) * mm, "radius": 0.64 * mm});
            skCircle(sketch, "E32.15.0.9", {"center": v(-7.11, -2.18) * mm, "radius": 0.64 * mm});
            skCircle(sketch, "E32.15.0.10", {"center": v(-3.56, -2.18) * mm, "radius": 0.64 * mm});
            skCircle(sketch, "E32.15.0.11", {"center": v(-10.67, -2.18) * mm, "radius": 0.64 * mm});
            skCircle(sketch, "E32.15.0.12", {"center": v(-14.22, -2.18) * mm, "radius": 0.64 * mm});
            skCircle(sketch, "E32.15.0.13", {"center": v(-21.34, -2.18) * mm, "radius": 0.64 * mm});
            skCircle(sketch, "E32.15.0.14", {"center": v(-24.9, -2.18) * mm, "radius": 0.64 * mm});
            skCircle(sketch, "E32.15.0.15", {"center": v(-28.45, -2.18) * mm, "radius": 0.64 * mm});
            skCircle(sketch, "E32.15.0.16", {"center": v(28.45, -2.18) * mm, "radius": 0.64 * mm});
            skCircle(sketch, "E32.15.0.17", {"center": v(7.11, -2.18) * mm, "radius": 0.64 * mm});
            skCircle(sketch, "E32.15.0.18", {"center": v(32, -2.18) * mm, "radius": 0.64 * mm});
            skCircle(sketch, "E32.15.0.19", {"center": v(35.56, -2.18) * mm, "radius": 0.64 * mm});
            skCircle(sketch, "E32.15.0.20", {"center": v(-17.78, -2.18) * mm, "radius": 0.64 * mm});
            skCircle(sketch, "E32.15.0.21", {"center": v(0, -2.18) * mm, "radius": 0.64 * mm});
            skCircle(sketch, "E32.15.0.22", {"center": v(24.9, -2.18) * mm, "radius": 0.64 * mm});
            skCircle(sketch, "E32.15.0.23", {"center": v(-42.67, -2.18) * mm, "radius": 0.64 * mm});
            skLineSegment(sketch, "E32.15.0.24", {"start": v(-42.67, -2.18) * mm, "end": v(-39.12, -2.18) * mm, "construction": true});
            skCircle(sketch, "E32.15.0.25", {"center": v(-39.12, -2.18) * mm, "radius": 0.64 * mm});
            skCircle(sketch, "E32.16.0.0", {"center": v(39.12, -5.84) * mm, "radius": 0.64 * mm});
            skCircle(sketch, "E32.16.0.1", {"center": v(14.22, -5.84) * mm, "radius": 0.64 * mm});
            skCircle(sketch, "E32.16.0.2", {"center": v(-32, -5.84) * mm, "radius": 0.64 * mm});
            skCircle(sketch, "E32.16.0.3", {"center": v(10.67, -5.84) * mm, "radius": 0.64 * mm});
            skCircle(sketch, "E32.16.0.4", {"center": v(-35.56, -5.84) * mm, "radius": 0.64 * mm});
            skCircle(sketch, "E32.16.0.5", {"center": v(17.78, -5.84) * mm, "radius": 0.64 * mm});
            skCircle(sketch, "E32.16.0.6", {"center": v(3.56, -5.84) * mm, "radius": 0.64 * mm});
            skCircle(sketch, "E32.16.0.7", {"center": v(21.34, -5.84) * mm, "radius": 0.64 * mm});
            skCircle(sketch, "E32.16.0.8", {"center": v(42.67, -5.84) * mm, "radius": 0.64 * mm});
            skCircle(sketch, "E32.16.0.9", {"center": v(-7.11, -5.84) * mm, "radius": 0.64 * mm});
            skCircle(sketch, "E32.16.0.10", {"center": v(-3.56, -5.84) * mm, "radius": 0.64 * mm});
            skCircle(sketch, "E32.16.0.11", {"center": v(-10.67, -5.84) * mm, "radius": 0.64 * mm});
            skCircle(sketch, "E32.16.0.12", {"center": v(-14.22, -5.84) * mm, "radius": 0.64 * mm});
            skCircle(sketch, "E32.16.0.13", {"center": v(-21.34, -5.84) * mm, "radius": 0.64 * mm});
            skCircle(sketch, "E32.16.0.14", {"center": v(-24.9, -5.84) * mm, "radius": 0.64 * mm});
            skCircle(sketch, "E32.16.0.15", {"center": v(-28.45, -5.84) * mm, "radius": 0.64 * mm});
            skCircle(sketch, "E32.16.0.16", {"center": v(28.45, -5.84) * mm, "radius": 0.64 * mm});
            skCircle(sketch, "E32.16.0.17", {"center": v(7.11, -5.84) * mm, "radius": 0.64 * mm});
            skCircle(sketch, "E32.16.0.18", {"center": v(32, -5.84) * mm, "radius": 0.64 * mm});
            skCircle(sketch, "E32.16.0.19", {"center": v(35.56, -5.84) * mm, "radius": 0.64 * mm});
            skCircle(sketch, "E32.16.0.20", {"center": v(-17.78, -5.84) * mm, "radius": 0.64 * mm});
            skCircle(sketch, "E32.16.0.21", {"center": v(0, -5.84) * mm, "radius": 0.64 * mm});
            skCircle(sketch, "E32.16.0.22", {"center": v(24.9, -5.84) * mm, "radius": 0.64 * mm});
            skCircle(sketch, "E32.16.0.23", {"center": v(-42.67, -5.84) * mm, "radius": 0.64 * mm});
            skLineSegment(sketch, "E32.16.0.24", {"start": v(-42.67, -5.84) * mm, "end": v(-39.12, -5.84) * mm, "construction": true});
            skCircle(sketch, "E32.16.0.25", {"center": v(-39.12, -5.84) * mm, "radius": 0.64 * mm});
            skCircle(sketch, "E32.17.0.0", {"center": v(39.12, -9.5) * mm, "radius": 0.64 * mm});
            skCircle(sketch, "E32.17.0.1", {"center": v(14.22, -9.5) * mm, "radius": 0.64 * mm});
            skCircle(sketch, "E32.17.0.2", {"center": v(-32, -9.5) * mm, "radius": 0.64 * mm});
            skCircle(sketch, "E32.17.0.3", {"center": v(10.67, -9.5) * mm, "radius": 0.64 * mm});
            skCircle(sketch, "E32.17.0.4", {"center": v(-35.56, -9.5) * mm, "radius": 0.64 * mm});
            skCircle(sketch, "E32.17.0.5", {"center": v(17.78, -9.5) * mm, "radius": 0.64 * mm});
            skCircle(sketch, "E32.17.0.6", {"center": v(3.56, -9.5) * mm, "radius": 0.64 * mm});
            skCircle(sketch, "E32.17.0.7", {"center": v(21.34, -9.5) * mm, "radius": 0.64 * mm});
            skCircle(sketch, "E32.17.0.8", {"center": v(42.67, -9.5) * mm, "radius": 0.64 * mm});
            skCircle(sketch, "E32.17.0.9", {"center": v(-7.11, -9.5) * mm, "radius": 0.64 * mm});
            skCircle(sketch, "E32.17.0.10", {"center": v(-3.56, -9.5) * mm, "radius": 0.64 * mm});
            skCircle(sketch, "E32.17.0.11", {"center": v(-10.67, -9.5) * mm, "radius": 0.64 * mm});
            skCircle(sketch, "E32.17.0.12", {"center": v(-14.22, -9.5) * mm, "radius": 0.64 * mm});
            skCircle(sketch, "E32.17.0.13", {"center": v(-21.34, -9.5) * mm, "radius": 0.64 * mm});
            skCircle(sketch, "E32.17.0.14", {"center": v(-24.9, -9.5) * mm, "radius": 0.64 * mm});
            skCircle(sketch, "E32.17.0.15", {"center": v(-28.45, -9.5) * mm, "radius": 0.64 * mm});
            skCircle(sketch, "E32.17.0.16", {"center": v(28.45, -9.5) * mm, "radius": 0.64 * mm});
            skCircle(sketch, "E32.17.0.17", {"center": v(7.11, -9.5) * mm, "radius": 0.64 * mm});
            skCircle(sketch, "E32.17.0.18", {"center": v(32, -9.5) * mm, "radius": 0.64 * mm});
            skCircle(sketch, "E32.17.0.19", {"center": v(35.56, -9.5) * mm, "radius": 0.64 * mm});
            skCircle(sketch, "E32.17.0.20", {"center": v(-17.78, -9.5) * mm, "radius": 0.64 * mm});
            skCircle(sketch, "E32.17.0.21", {"center": v(0, -9.5) * mm, "radius": 0.64 * mm});
            skCircle(sketch, "E32.17.0.22", {"center": v(24.9, -9.5) * mm, "radius": 0.64 * mm});
            skCircle(sketch, "E32.17.0.23", {"center": v(-42.67, -9.5) * mm, "radius": 0.64 * mm});
            skLineSegment(sketch, "E32.17.0.24", {"start": v(-42.67, -9.5) * mm, "end": v(-39.12, -9.5) * mm, "construction": true});
            skCircle(sketch, "E32.17.0.25", {"center": v(-39.12, -9.5) * mm, "radius": 0.64 * mm});
            skCircle(sketch, "E32.18.0.0", {"center": v(39.12, -13.16) * mm, "radius": 0.64 * mm});
            skCircle(sketch, "E32.18.0.1", {"center": v(14.22, -13.16) * mm, "radius": 0.64 * mm});
            skCircle(sketch, "E32.18.0.2", {"center": v(-32, -13.16) * mm, "radius": 0.64 * mm});
            skCircle(sketch, "E32.18.0.3", {"center": v(10.67, -13.16) * mm, "radius": 0.64 * mm});
            skCircle(sketch, "E32.18.0.4", {"center": v(-35.56, -13.16) * mm, "radius": 0.64 * mm});
            skCircle(sketch, "E32.18.0.5", {"center": v(17.78, -13.16) * mm, "radius": 0.64 * mm});
            skCircle(sketch, "E32.18.0.6", {"center": v(3.56, -13.16) * mm, "radius": 0.64 * mm});
            skCircle(sketch, "E32.18.0.7", {"center": v(21.34, -13.16) * mm, "radius": 0.64 * mm});
            skCircle(sketch, "E32.18.0.8", {"center": v(42.67, -13.16) * mm, "radius": 0.64 * mm});
            skCircle(sketch, "E32.18.0.9", {"center": v(-7.11, -13.16) * mm, "radius": 0.64 * mm});
            skCircle(sketch, "E32.18.0.10", {"center": v(-3.56, -13.16) * mm, "radius": 0.64 * mm});
            skCircle(sketch, "E32.18.0.11", {"center": v(-10.67, -13.16) * mm, "radius": 0.64 * mm});
            skCircle(sketch, "E32.18.0.12", {"center": v(-14.22, -13.16) * mm, "radius": 0.64 * mm});
            skCircle(sketch, "E32.18.0.13", {"center": v(-21.34, -13.16) * mm, "radius": 0.64 * mm});
            skCircle(sketch, "E32.18.0.14", {"center": v(-24.9, -13.16) * mm, "radius": 0.64 * mm});
            skCircle(sketch, "E32.18.0.15", {"center": v(-28.45, -13.16) * mm, "radius": 0.64 * mm});
            skCircle(sketch, "E32.18.0.16", {"center": v(28.45, -13.16) * mm, "radius": 0.64 * mm});
            skCircle(sketch, "E32.18.0.17", {"center": v(7.11, -13.16) * mm, "radius": 0.64 * mm});
            skCircle(sketch, "E32.18.0.18", {"center": v(32, -13.16) * mm, "radius": 0.64 * mm});
            skCircle(sketch, "E32.18.0.19", {"center": v(35.56, -13.16) * mm, "radius": 0.64 * mm});
            skCircle(sketch, "E32.18.0.20", {"center": v(-17.78, -13.16) * mm, "radius": 0.64 * mm});
            skCircle(sketch, "E32.18.0.21", {"center": v(0, -13.16) * mm, "radius": 0.64 * mm});
            skCircle(sketch, "E32.18.0.22", {"center": v(24.9, -13.16) * mm, "radius": 0.64 * mm});
            skCircle(sketch, "E32.18.0.23", {"center": v(-42.67, -13.16) * mm, "radius": 0.64 * mm});
            skLineSegment(sketch, "E32.18.0.24", {"start": v(-42.67, -13.16) * mm, "end": v(-39.12, -13.16) * mm, "construction": true});
            skCircle(sketch, "E32.18.0.25", {"center": v(-39.12, -13.16) * mm, "radius": 0.64 * mm});
            skCircle(sketch, "E32.19.0.0", {"center": v(39.12, -16.81) * mm, "radius": 0.64 * mm});
            skCircle(sketch, "E32.19.0.1", {"center": v(14.22, -16.81) * mm, "radius": 0.64 * mm});
            skCircle(sketch, "E32.19.0.2", {"center": v(-32, -16.81) * mm, "radius": 0.64 * mm});
            skCircle(sketch, "E32.19.0.3", {"center": v(10.67, -16.81) * mm, "radius": 0.64 * mm});
            skCircle(sketch, "E32.19.0.4", {"center": v(-35.56, -16.81) * mm, "radius": 0.64 * mm});
            skCircle(sketch, "E32.19.0.5", {"center": v(17.78, -16.81) * mm, "radius": 0.64 * mm});
            skCircle(sketch, "E32.19.0.6", {"center": v(3.56, -16.81) * mm, "radius": 0.64 * mm});
            skCircle(sketch, "E32.19.0.7", {"center": v(21.34, -16.81) * mm, "radius": 0.64 * mm});
            skCircle(sketch, "E32.19.0.8", {"center": v(42.67, -16.81) * mm, "radius": 0.64 * mm});
            skCircle(sketch, "E32.19.0.9", {"center": v(-7.11, -16.81) * mm, "radius": 0.64 * mm});
            skCircle(sketch, "E32.19.0.10", {"center": v(-3.56, -16.81) * mm, "radius": 0.64 * mm});
            skCircle(sketch, "E32.19.0.11", {"center": v(-10.67, -16.81) * mm, "radius": 0.64 * mm});
            skCircle(sketch, "E32.19.0.12", {"center": v(-14.22, -16.81) * mm, "radius": 0.64 * mm});
            skCircle(sketch, "E32.19.0.13", {"center": v(-21.34, -16.81) * mm, "radius": 0.64 * mm});
            skCircle(sketch, "E32.19.0.14", {"center": v(-24.9, -16.81) * mm, "radius": 0.64 * mm});
            skCircle(sketch, "E32.19.0.15", {"center": v(-28.45, -16.81) * mm, "radius": 0.64 * mm});
            skCircle(sketch, "E32.19.0.16", {"center": v(28.45, -16.81) * mm, "radius": 0.64 * mm});
            skCircle(sketch, "E32.19.0.17", {"center": v(7.11, -16.81) * mm, "radius": 0.64 * mm});
            skCircle(sketch, "E32.19.0.18", {"center": v(32, -16.81) * mm, "radius": 0.64 * mm});
            skCircle(sketch, "E32.19.0.19", {"center": v(35.56, -16.81) * mm, "radius": 0.64 * mm});
            skCircle(sketch, "E32.19.0.20", {"center": v(-17.78, -16.81) * mm, "radius": 0.64 * mm});
            skCircle(sketch, "E32.19.0.21", {"center": v(0, -16.81) * mm, "radius": 0.64 * mm});
            skCircle(sketch, "E32.19.0.22", {"center": v(24.9, -16.81) * mm, "radius": 0.64 * mm});
            skCircle(sketch, "E32.19.0.23", {"center": v(-42.67, -16.81) * mm, "radius": 0.64 * mm});
            skLineSegment(sketch, "E32.19.0.24", {"start": v(-42.67, -16.81) * mm, "end": v(-39.12, -16.81) * mm, "construction": true});
            skCircle(sketch, "E32.19.0.25", {"center": v(-39.12, -16.81) * mm, "radius": 0.64 * mm});
            skCircle(sketch, "E32.20.0.0", {"center": v(39.12, -20.47) * mm, "radius": 0.64 * mm});
            skCircle(sketch, "E32.20.0.1", {"center": v(14.22, -20.47) * mm, "radius": 0.64 * mm});
            skCircle(sketch, "E32.20.0.2", {"center": v(-32, -20.47) * mm, "radius": 0.64 * mm});
            skCircle(sketch, "E32.20.0.3", {"center": v(10.67, -20.47) * mm, "radius": 0.64 * mm});
            skCircle(sketch, "E32.20.0.4", {"center": v(-35.56, -20.47) * mm, "radius": 0.64 * mm});
            skCircle(sketch, "E32.20.0.5", {"center": v(17.78, -20.47) * mm, "radius": 0.64 * mm});
            skCircle(sketch, "E32.20.0.6", {"center": v(3.56, -20.47) * mm, "radius": 0.64 * mm});
            skCircle(sketch, "E32.20.0.7", {"center": v(21.34, -20.47) * mm, "radius": 0.64 * mm});
            skCircle(sketch, "E32.20.0.8", {"center": v(42.67, -20.47) * mm, "radius": 0.64 * mm});
            skCircle(sketch, "E32.20.0.9", {"center": v(-7.11, -20.47) * mm, "radius": 0.64 * mm});
            skCircle(sketch, "E32.20.0.10", {"center": v(-3.56, -20.47) * mm, "radius": 0.64 * mm});
            skCircle(sketch, "E32.20.0.11", {"center": v(-10.67, -20.47) * mm, "radius": 0.64 * mm});
            skCircle(sketch, "E32.20.0.12", {"center": v(-14.22, -20.47) * mm, "radius": 0.64 * mm});
            skCircle(sketch, "E32.20.0.13", {"center": v(-21.34, -20.47) * mm, "radius": 0.64 * mm});
            skCircle(sketch, "E32.20.0.14", {"center": v(-24.9, -20.47) * mm, "radius": 0.64 * mm});
            skCircle(sketch, "E32.20.0.15", {"center": v(-28.45, -20.47) * mm, "radius": 0.64 * mm});
            skCircle(sketch, "E32.20.0.16", {"center": v(28.45, -20.47) * mm, "radius": 0.64 * mm});
            skCircle(sketch, "E32.20.0.17", {"center": v(7.11, -20.47) * mm, "radius": 0.64 * mm});
            skCircle(sketch, "E32.20.0.18", {"center": v(32, -20.47) * mm, "radius": 0.64 * mm});
            skCircle(sketch, "E32.20.0.19", {"center": v(35.56, -20.47) * mm, "radius": 0.64 * mm});
            skCircle(sketch, "E32.20.0.20", {"center": v(-17.78, -20.47) * mm, "radius": 0.64 * mm});
            skCircle(sketch, "E32.20.0.21", {"center": v(0, -20.47) * mm, "radius": 0.64 * mm});
            skCircle(sketch, "E32.20.0.22", {"center": v(24.9, -20.47) * mm, "radius": 0.64 * mm});
            skCircle(sketch, "E32.20.0.23", {"center": v(-42.67, -20.47) * mm, "radius": 0.64 * mm});
            skLineSegment(sketch, "E32.20.0.24", {"start": v(-42.67, -20.47) * mm, "end": v(-39.12, -20.47) * mm, "construction": true});
            skCircle(sketch, "E32.20.0.25", {"center": v(-39.12, -20.47) * mm, "radius": 0.64 * mm});
            skCircle(sketch, "E32.21.0.0", {"center": v(39.12, -24.13) * mm, "radius": 0.64 * mm});
            skCircle(sketch, "E32.21.0.1", {"center": v(14.22, -24.13) * mm, "radius": 0.64 * mm});
            skCircle(sketch, "E32.21.0.2", {"center": v(-32, -24.13) * mm, "radius": 0.64 * mm});
            skCircle(sketch, "E32.21.0.3", {"center": v(10.67, -24.13) * mm, "radius": 0.64 * mm});
            skCircle(sketch, "E32.21.0.4", {"center": v(-35.56, -24.13) * mm, "radius": 0.64 * mm});
            skCircle(sketch, "E32.21.0.5", {"center": v(17.78, -24.13) * mm, "radius": 0.64 * mm});
            skCircle(sketch, "E32.21.0.6", {"center": v(3.56, -24.13) * mm, "radius": 0.64 * mm});
            skCircle(sketch, "E32.21.0.7", {"center": v(21.34, -24.13) * mm, "radius": 0.64 * mm});
            skCircle(sketch, "E32.21.0.8", {"center": v(42.67, -24.13) * mm, "radius": 0.64 * mm});
            skCircle(sketch, "E32.21.0.9", {"center": v(-7.11, -24.13) * mm, "radius": 0.64 * mm});
            skCircle(sketch, "E32.21.0.10", {"center": v(-3.56, -24.13) * mm, "radius": 0.64 * mm});
            skCircle(sketch, "E32.21.0.11", {"center": v(-10.67, -24.13) * mm, "radius": 0.64 * mm});
            skCircle(sketch, "E32.21.0.12", {"center": v(-14.22, -24.13) * mm, "radius": 0.64 * mm});
            skCircle(sketch, "E32.21.0.13", {"center": v(-21.34, -24.13) * mm, "radius": 0.64 * mm});
            skCircle(sketch, "E32.21.0.14", {"center": v(-24.9, -24.13) * mm, "radius": 0.64 * mm});
            skCircle(sketch, "E32.21.0.15", {"center": v(-28.45, -24.13) * mm, "radius": 0.64 * mm});
            skCircle(sketch, "E32.21.0.16", {"center": v(28.45, -24.13) * mm, "radius": 0.64 * mm});
            skCircle(sketch, "E32.21.0.17", {"center": v(7.11, -24.13) * mm, "radius": 0.64 * mm});
            skCircle(sketch, "E32.21.0.18", {"center": v(32, -24.13) * mm, "radius": 0.64 * mm});
            skCircle(sketch, "E32.21.0.19", {"center": v(35.56, -24.13) * mm, "radius": 0.64 * mm});
            skCircle(sketch, "E32.21.0.20", {"center": v(-17.78, -24.13) * mm, "radius": 0.64 * mm});
            skCircle(sketch, "E32.21.0.21", {"center": v(0, -24.13) * mm, "radius": 0.64 * mm});
            skCircle(sketch, "E32.21.0.22", {"center": v(24.9, -24.13) * mm, "radius": 0.64 * mm});
            skCircle(sketch, "E32.21.0.23", {"center": v(-42.67, -24.13) * mm, "radius": 0.64 * mm});
            skLineSegment(sketch, "E32.21.0.24", {"start": v(-42.67, -24.13) * mm, "end": v(-39.12, -24.13) * mm, "construction": true});
            skCircle(sketch, "E32.21.0.25", {"center": v(-39.12, -24.13) * mm, "radius": 0.64 * mm});
            skCircle(sketch, "E32.22.0.0", {"center": v(39.12, -27.79) * mm, "radius": 0.64 * mm});
            skCircle(sketch, "E32.22.0.1", {"center": v(14.22, -27.79) * mm, "radius": 0.64 * mm});
            skCircle(sketch, "E32.22.0.2", {"center": v(-32, -27.79) * mm, "radius": 0.64 * mm});
            skCircle(sketch, "E32.22.0.3", {"center": v(10.67, -27.79) * mm, "radius": 0.64 * mm});
            skCircle(sketch, "E32.22.0.4", {"center": v(-35.56, -27.79) * mm, "radius": 0.64 * mm});
            skCircle(sketch, "E32.22.0.5", {"center": v(17.78, -27.79) * mm, "radius": 0.64 * mm});
            skCircle(sketch, "E32.22.0.6", {"center": v(3.56, -27.79) * mm, "radius": 0.64 * mm});
            skCircle(sketch, "E32.22.0.7", {"center": v(21.34, -27.79) * mm, "radius": 0.64 * mm});
            skCircle(sketch, "E32.22.0.8", {"center": v(42.67, -27.79) * mm, "radius": 0.64 * mm});
            skCircle(sketch, "E32.22.0.9", {"center": v(-7.11, -27.79) * mm, "radius": 0.64 * mm});
            skCircle(sketch, "E32.22.0.10", {"center": v(-3.56, -27.79) * mm, "radius": 0.64 * mm});
            skCircle(sketch, "E32.22.0.11", {"center": v(-10.67, -27.79) * mm, "radius": 0.64 * mm});
            skCircle(sketch, "E32.22.0.12", {"center": v(-14.22, -27.79) * mm, "radius": 0.64 * mm});
            skCircle(sketch, "E32.22.0.13", {"center": v(-21.34, -27.79) * mm, "radius": 0.64 * mm});
            skCircle(sketch, "E32.22.0.14", {"center": v(-24.9, -27.79) * mm, "radius": 0.64 * mm});
            skCircle(sketch, "E32.22.0.15", {"center": v(-28.45, -27.79) * mm, "radius": 0.64 * mm});
            skCircle(sketch, "E32.22.0.16", {"center": v(28.45, -27.79) * mm, "radius": 0.64 * mm});
            skCircle(sketch, "E32.22.0.17", {"center": v(7.11, -27.79) * mm, "radius": 0.64 * mm});
            skCircle(sketch, "E32.22.0.18", {"center": v(32, -27.79) * mm, "radius": 0.64 * mm});
            skCircle(sketch, "E32.22.0.19", {"center": v(35.56, -27.79) * mm, "radius": 0.64 * mm});
            skCircle(sketch, "E32.22.0.20", {"center": v(-17.78, -27.79) * mm, "radius": 0.64 * mm});
            skCircle(sketch, "E32.22.0.21", {"center": v(0, -27.79) * mm, "radius": 0.64 * mm});
            skCircle(sketch, "E32.22.0.22", {"center": v(24.9, -27.79) * mm, "radius": 0.64 * mm});
            skCircle(sketch, "E32.22.0.23", {"center": v(-42.67, -27.79) * mm, "radius": 0.64 * mm});
            skLineSegment(sketch, "E32.22.0.24", {"start": v(-42.67, -27.79) * mm, "end": v(-39.12, -27.79) * mm, "construction": true});
            skCircle(sketch, "E32.22.0.25", {"center": v(-39.12, -27.79) * mm, "radius": 0.64 * mm});
            skCircle(sketch, "E32.23.0.0", {"center": v(39.12, -31.45) * mm, "radius": 0.64 * mm});
            skCircle(sketch, "E32.23.0.1", {"center": v(14.22, -31.45) * mm, "radius": 0.64 * mm});
            skCircle(sketch, "E32.23.0.2", {"center": v(-32, -31.45) * mm, "radius": 0.64 * mm});
            skCircle(sketch, "E32.23.0.3", {"center": v(10.67, -31.45) * mm, "radius": 0.64 * mm});
            skCircle(sketch, "E32.23.0.4", {"center": v(-35.56, -31.45) * mm, "radius": 0.64 * mm});
            skCircle(sketch, "E32.23.0.5", {"center": v(17.78, -31.45) * mm, "radius": 0.64 * mm});
            skCircle(sketch, "E32.23.0.6", {"center": v(3.56, -31.45) * mm, "radius": 0.64 * mm});
            skCircle(sketch, "E32.23.0.7", {"center": v(21.34, -31.45) * mm, "radius": 0.64 * mm});
            skCircle(sketch, "E32.23.0.8", {"center": v(42.67, -31.45) * mm, "radius": 0.64 * mm});
            skCircle(sketch, "E32.23.0.9", {"center": v(-7.11, -31.45) * mm, "radius": 0.64 * mm});
            skCircle(sketch, "E32.23.0.10", {"center": v(-3.56, -31.45) * mm, "radius": 0.64 * mm});
            skCircle(sketch, "E32.23.0.11", {"center": v(-10.67, -31.45) * mm, "radius": 0.64 * mm});
            skCircle(sketch, "E32.23.0.12", {"center": v(-14.22, -31.45) * mm, "radius": 0.64 * mm});
            skCircle(sketch, "E32.23.0.13", {"center": v(-21.34, -31.45) * mm, "radius": 0.64 * mm});
            skCircle(sketch, "E32.23.0.14", {"center": v(-24.9, -31.45) * mm, "radius": 0.64 * mm});
            skCircle(sketch, "E32.23.0.15", {"center": v(-28.45, -31.45) * mm, "radius": 0.64 * mm});
            skCircle(sketch, "E32.23.0.16", {"center": v(28.45, -31.45) * mm, "radius": 0.64 * mm});
            skCircle(sketch, "E32.23.0.17", {"center": v(7.11, -31.45) * mm, "radius": 0.64 * mm});
            skCircle(sketch, "E32.23.0.18", {"center": v(32, -31.45) * mm, "radius": 0.64 * mm});
            skCircle(sketch, "E32.23.0.19", {"center": v(35.56, -31.45) * mm, "radius": 0.64 * mm});
            skCircle(sketch, "E32.23.0.20", {"center": v(-17.78, -31.45) * mm, "radius": 0.64 * mm});
            skCircle(sketch, "E32.23.0.21", {"center": v(0, -31.45) * mm, "radius": 0.64 * mm});
            skCircle(sketch, "E32.23.0.22", {"center": v(24.9, -31.45) * mm, "radius": 0.64 * mm});
            skCircle(sketch, "E32.23.0.23", {"center": v(-42.67, -31.45) * mm, "radius": 0.64 * mm});
            skLineSegment(sketch, "E32.23.0.24", {"start": v(-42.67, -31.45) * mm, "end": v(-39.12, -31.45) * mm, "construction": true});
            skCircle(sketch, "E32.23.0.25", {"center": v(-39.12, -31.45) * mm, "radius": 0.64 * mm});
            skCircle(sketch, "E32.24.0.0", {"center": v(39.12, -35.1) * mm, "radius": 0.64 * mm});
            skCircle(sketch, "E32.24.0.1", {"center": v(14.22, -35.1) * mm, "radius": 0.64 * mm});
            skCircle(sketch, "E32.24.0.2", {"center": v(-32, -35.1) * mm, "radius": 0.64 * mm});
            skCircle(sketch, "E32.24.0.3", {"center": v(10.67, -35.1) * mm, "radius": 0.64 * mm});
            skCircle(sketch, "E32.24.0.4", {"center": v(-35.56, -35.1) * mm, "radius": 0.64 * mm});
            skCircle(sketch, "E32.24.0.5", {"center": v(17.78, -35.1) * mm, "radius": 0.64 * mm});
            skCircle(sketch, "E32.24.0.6", {"center": v(3.56, -35.1) * mm, "radius": 0.64 * mm});
            skCircle(sketch, "E32.24.0.7", {"center": v(21.34, -35.1) * mm, "radius": 0.64 * mm});
            skCircle(sketch, "E32.24.0.8", {"center": v(42.67, -35.1) * mm, "radius": 0.64 * mm});
            skCircle(sketch, "E32.24.0.9", {"center": v(-7.11, -35.1) * mm, "radius": 0.64 * mm});
            skCircle(sketch, "E32.24.0.10", {"center": v(-3.56, -35.1) * mm, "radius": 0.64 * mm});
            skCircle(sketch, "E32.24.0.11", {"center": v(-10.67, -35.1) * mm, "radius": 0.64 * mm});
            skCircle(sketch, "E32.24.0.12", {"center": v(-14.22, -35.1) * mm, "radius": 0.64 * mm});
            skCircle(sketch, "E32.24.0.13", {"center": v(-21.34, -35.1) * mm, "radius": 0.64 * mm});
            skCircle(sketch, "E32.24.0.14", {"center": v(-24.9, -35.1) * mm, "radius": 0.64 * mm});
            skCircle(sketch, "E32.24.0.15", {"center": v(-28.45, -35.1) * mm, "radius": 0.64 * mm});
            skCircle(sketch, "E32.24.0.16", {"center": v(28.45, -35.1) * mm, "radius": 0.64 * mm});
            skCircle(sketch, "E32.24.0.17", {"center": v(7.11, -35.1) * mm, "radius": 0.64 * mm});
            skCircle(sketch, "E32.24.0.18", {"center": v(32, -35.1) * mm, "radius": 0.64 * mm});
            skCircle(sketch, "E32.24.0.19", {"center": v(35.56, -35.1) * mm, "radius": 0.64 * mm});
            skCircle(sketch, "E32.24.0.20", {"center": v(-17.78, -35.1) * mm, "radius": 0.64 * mm});
            skCircle(sketch, "E32.24.0.21", {"center": v(0, -35.1) * mm, "radius": 0.64 * mm});
            skCircle(sketch, "E32.24.0.22", {"center": v(24.9, -35.1) * mm, "radius": 0.64 * mm});
            skCircle(sketch, "E32.24.0.23", {"center": v(-42.67, -35.1) * mm, "radius": 0.64 * mm});
            skLineSegment(sketch, "E32.24.0.24", {"start": v(-42.67, -35.1) * mm, "end": v(-39.12, -35.1) * mm, "construction": true});
            skCircle(sketch, "E32.24.0.25", {"center": v(-39.12, -35.1) * mm, "radius": 0.64 * mm});
            skCircle(sketch, "E32.25.0.0", {"center": v(39.12, -38.76) * mm, "radius": 0.64 * mm});
            skCircle(sketch, "E32.25.0.1", {"center": v(14.22, -38.76) * mm, "radius": 0.64 * mm});
            skCircle(sketch, "E32.25.0.2", {"center": v(-32, -38.76) * mm, "radius": 0.64 * mm});
            skCircle(sketch, "E32.25.0.3", {"center": v(10.67, -38.76) * mm, "radius": 0.64 * mm});
            skCircle(sketch, "E32.25.0.4", {"center": v(-35.56, -38.76) * mm, "radius": 0.64 * mm});
            skCircle(sketch, "E32.25.0.5", {"center": v(17.78, -38.76) * mm, "radius": 0.64 * mm});
            skCircle(sketch, "E32.25.0.6", {"center": v(3.56, -38.76) * mm, "radius": 0.64 * mm});
            skCircle(sketch, "E32.25.0.7", {"center": v(21.34, -38.76) * mm, "radius": 0.64 * mm});
            skCircle(sketch, "E32.25.0.8", {"center": v(42.67, -38.76) * mm, "radius": 0.64 * mm});
            skCircle(sketch, "E32.25.0.9", {"center": v(-7.11, -38.76) * mm, "radius": 0.64 * mm});
            skCircle(sketch, "E32.25.0.10", {"center": v(-3.56, -38.76) * mm, "radius": 0.64 * mm});
            skCircle(sketch, "E32.25.0.11", {"center": v(-10.67, -38.76) * mm, "radius": 0.64 * mm});
            skCircle(sketch, "E32.25.0.12", {"center": v(-14.22, -38.76) * mm, "radius": 0.64 * mm});
            skCircle(sketch, "E32.25.0.13", {"center": v(-21.34, -38.76) * mm, "radius": 0.64 * mm});
            skCircle(sketch, "E32.25.0.14", {"center": v(-24.9, -38.76) * mm, "radius": 0.64 * mm});
            skCircle(sketch, "E32.25.0.15", {"center": v(-28.45, -38.76) * mm, "radius": 0.64 * mm});
            skCircle(sketch, "E32.25.0.16", {"center": v(28.45, -38.76) * mm, "radius": 0.64 * mm});
            skCircle(sketch, "E32.25.0.17", {"center": v(7.11, -38.76) * mm, "radius": 0.64 * mm});
            skCircle(sketch, "E32.25.0.18", {"center": v(32, -38.76) * mm, "radius": 0.64 * mm});
            skCircle(sketch, "E32.25.0.19", {"center": v(35.56, -38.76) * mm, "radius": 0.64 * mm});
            skCircle(sketch, "E32.25.0.20", {"center": v(-17.78, -38.76) * mm, "radius": 0.64 * mm});
            skCircle(sketch, "E32.25.0.21", {"center": v(0, -38.76) * mm, "radius": 0.64 * mm});
            skCircle(sketch, "E32.25.0.22", {"center": v(24.9, -38.76) * mm, "radius": 0.64 * mm});
            skCircle(sketch, "E32.25.0.23", {"center": v(-42.67, -38.76) * mm, "radius": 0.64 * mm});
            skLineSegment(sketch, "E32.25.0.24", {"start": v(-42.67, -38.76) * mm, "end": v(-39.12, -38.76) * mm, "construction": true});
            skCircle(sketch, "E32.25.0.25", {"center": v(-39.12, -38.76) * mm, "radius": 0.64 * mm});
            skCircle(sketch, "E32.26.0.0", {"center": v(39.12, -42.42) * mm, "radius": 0.64 * mm});
            skCircle(sketch, "E32.26.0.1", {"center": v(14.22, -42.42) * mm, "radius": 0.64 * mm});
            skCircle(sketch, "E32.26.0.2", {"center": v(-32, -42.42) * mm, "radius": 0.64 * mm});
            skCircle(sketch, "E32.26.0.3", {"center": v(10.67, -42.42) * mm, "radius": 0.64 * mm});
            skCircle(sketch, "E32.26.0.4", {"center": v(-35.56, -42.42) * mm, "radius": 0.64 * mm});
            skCircle(sketch, "E32.26.0.5", {"center": v(17.78, -42.42) * mm, "radius": 0.64 * mm});
            skCircle(sketch, "E32.26.0.6", {"center": v(3.56, -42.42) * mm, "radius": 0.64 * mm});
            skCircle(sketch, "E32.26.0.7", {"center": v(21.34, -42.42) * mm, "radius": 0.64 * mm});
            skCircle(sketch, "E32.26.0.8", {"center": v(42.67, -42.42) * mm, "radius": 0.64 * mm});
            skCircle(sketch, "E32.26.0.9", {"center": v(-7.11, -42.42) * mm, "radius": 0.64 * mm});
            skCircle(sketch, "E32.26.0.10", {"center": v(-3.56, -42.42) * mm, "radius": 0.64 * mm});
            skCircle(sketch, "E32.26.0.11", {"center": v(-10.67, -42.42) * mm, "radius": 0.64 * mm});
            skCircle(sketch, "E32.26.0.12", {"center": v(-14.22, -42.42) * mm, "radius": 0.64 * mm});
            skCircle(sketch, "E32.26.0.13", {"center": v(-21.34, -42.42) * mm, "radius": 0.64 * mm});
            skCircle(sketch, "E32.26.0.14", {"center": v(-24.9, -42.42) * mm, "radius": 0.64 * mm});
            skCircle(sketch, "E32.26.0.15", {"center": v(-28.45, -42.42) * mm, "radius": 0.64 * mm});
            skCircle(sketch, "E32.26.0.16", {"center": v(28.45, -42.42) * mm, "radius": 0.64 * mm});
            skCircle(sketch, "E32.26.0.17", {"center": v(7.11, -42.42) * mm, "radius": 0.64 * mm});
            skCircle(sketch, "E32.26.0.18", {"center": v(32, -42.42) * mm, "radius": 0.64 * mm});
            skCircle(sketch, "E32.26.0.19", {"center": v(35.56, -42.42) * mm, "radius": 0.64 * mm});
            skCircle(sketch, "E32.26.0.20", {"center": v(-17.78, -42.42) * mm, "radius": 0.64 * mm});
            skCircle(sketch, "E32.26.0.21", {"center": v(0, -42.42) * mm, "radius": 0.64 * mm});
            skCircle(sketch, "E32.26.0.22", {"center": v(24.9, -42.42) * mm, "radius": 0.64 * mm});
            skCircle(sketch, "E32.26.0.23", {"center": v(-42.67, -42.42) * mm, "radius": 0.64 * mm});
            skLineSegment(sketch, "E32.26.0.24", {"start": v(-42.67, -42.42) * mm, "end": v(-39.12, -42.42) * mm, "construction": true});
            skCircle(sketch, "E32.26.0.25", {"center": v(-39.12, -42.42) * mm, "radius": 0.64 * mm});
            skCircle(sketch, "E32.27.0.0", {"center": v(39.12, -46.08) * mm, "radius": 0.64 * mm});
            skCircle(sketch, "E32.27.0.1", {"center": v(14.22, -46.08) * mm, "radius": 0.64 * mm});
            skCircle(sketch, "E32.27.0.2", {"center": v(-32, -46.08) * mm, "radius": 0.64 * mm});
            skCircle(sketch, "E32.27.0.3", {"center": v(10.67, -46.08) * mm, "radius": 0.64 * mm});
            skCircle(sketch, "E32.27.0.4", {"center": v(-35.56, -46.08) * mm, "radius": 0.64 * mm});
            skCircle(sketch, "E32.27.0.5", {"center": v(17.78, -46.08) * mm, "radius": 0.64 * mm});
            skCircle(sketch, "E32.27.0.6", {"center": v(3.56, -46.08) * mm, "radius": 0.64 * mm});
            skCircle(sketch, "E32.27.0.7", {"center": v(21.34, -46.08) * mm, "radius": 0.64 * mm});
            skCircle(sketch, "E32.27.0.8", {"center": v(42.67, -46.08) * mm, "radius": 0.64 * mm});
            skCircle(sketch, "E32.27.0.9", {"center": v(-7.11, -46.08) * mm, "radius": 0.64 * mm});
            skCircle(sketch, "E32.27.0.10", {"center": v(-3.56, -46.08) * mm, "radius": 0.64 * mm});
            skCircle(sketch, "E32.27.0.11", {"center": v(-10.67, -46.08) * mm, "radius": 0.64 * mm});
            skCircle(sketch, "E32.27.0.12", {"center": v(-14.22, -46.08) * mm, "radius": 0.64 * mm});
            skCircle(sketch, "E32.27.0.13", {"center": v(-21.34, -46.08) * mm, "radius": 0.64 * mm});
            skCircle(sketch, "E32.27.0.14", {"center": v(-24.9, -46.08) * mm, "radius": 0.64 * mm});
            skCircle(sketch, "E32.27.0.15", {"center": v(-28.45, -46.08) * mm, "radius": 0.64 * mm});
            skCircle(sketch, "E32.27.0.16", {"center": v(28.45, -46.08) * mm, "radius": 0.64 * mm});
            skCircle(sketch, "E32.27.0.17", {"center": v(7.11, -46.08) * mm, "radius": 0.64 * mm});
            skCircle(sketch, "E32.27.0.18", {"center": v(32, -46.08) * mm, "radius": 0.64 * mm});
            skCircle(sketch, "E32.27.0.19", {"center": v(35.56, -46.08) * mm, "radius": 0.64 * mm});
            skCircle(sketch, "E32.27.0.20", {"center": v(-17.78, -46.08) * mm, "radius": 0.64 * mm});
            skCircle(sketch, "E32.27.0.21", {"center": v(0, -46.08) * mm, "radius": 0.64 * mm});
            skCircle(sketch, "E32.27.0.22", {"center": v(24.9, -46.08) * mm, "radius": 0.64 * mm});
            skCircle(sketch, "E32.27.0.23", {"center": v(-42.67, -46.08) * mm, "radius": 0.64 * mm});
            skLineSegment(sketch, "E32.27.0.24", {"start": v(-42.67, -46.08) * mm, "end": v(-39.12, -46.08) * mm, "construction": true});
            skCircle(sketch, "E32.27.0.25", {"center": v(-39.12, -46.08) * mm, "radius": 0.64 * mm});
            skCircle(sketch, "E32.28.0.0", {"center": v(39.12, -49.73) * mm, "radius": 0.64 * mm});
            skCircle(sketch, "E32.28.0.1", {"center": v(14.22, -49.73) * mm, "radius": 0.64 * mm});
            skCircle(sketch, "E32.28.0.2", {"center": v(-32, -49.73) * mm, "radius": 0.64 * mm});
            skCircle(sketch, "E32.28.0.3", {"center": v(10.67, -49.73) * mm, "radius": 0.64 * mm});
            skCircle(sketch, "E32.28.0.4", {"center": v(-35.56, -49.73) * mm, "radius": 0.64 * mm});
            skCircle(sketch, "E32.28.0.5", {"center": v(17.78, -49.73) * mm, "radius": 0.64 * mm});
            skCircle(sketch, "E32.28.0.6", {"center": v(3.56, -49.73) * mm, "radius": 0.64 * mm});
            skCircle(sketch, "E32.28.0.7", {"center": v(21.34, -49.73) * mm, "radius": 0.64 * mm});
            skCircle(sketch, "E32.28.0.8", {"center": v(42.67, -49.73) * mm, "radius": 0.64 * mm});
            skCircle(sketch, "E32.28.0.9", {"center": v(-7.11, -49.73) * mm, "radius": 0.64 * mm});
            skCircle(sketch, "E32.28.0.10", {"center": v(-3.56, -49.73) * mm, "radius": 0.64 * mm});
            skCircle(sketch, "E32.28.0.11", {"center": v(-10.67, -49.73) * mm, "radius": 0.64 * mm});
            skCircle(sketch, "E32.28.0.12", {"center": v(-14.22, -49.73) * mm, "radius": 0.64 * mm});
            skCircle(sketch, "E32.28.0.13", {"center": v(-21.34, -49.73) * mm, "radius": 0.64 * mm});
            skCircle(sketch, "E32.28.0.14", {"center": v(-24.9, -49.73) * mm, "radius": 0.64 * mm});
            skCircle(sketch, "E32.28.0.15", {"center": v(-28.45, -49.73) * mm, "radius": 0.64 * mm});
            skCircle(sketch, "E32.28.0.16", {"center": v(28.45, -49.73) * mm, "radius": 0.64 * mm});
            skCircle(sketch, "E32.28.0.17", {"center": v(7.11, -49.73) * mm, "radius": 0.64 * mm});
            skCircle(sketch, "E32.28.0.18", {"center": v(32, -49.73) * mm, "radius": 0.64 * mm});
            skCircle(sketch, "E32.28.0.19", {"center": v(35.56, -49.73) * mm, "radius": 0.64 * mm});
            skCircle(sketch, "E32.28.0.20", {"center": v(-17.78, -49.73) * mm, "radius": 0.64 * mm});
            skCircle(sketch, "E32.28.0.21", {"center": v(0, -49.73) * mm, "radius": 0.64 * mm});
            skCircle(sketch, "E32.28.0.22", {"center": v(24.9, -49.73) * mm, "radius": 0.64 * mm});
            skCircle(sketch, "E32.28.0.23", {"center": v(-42.67, -49.73) * mm, "radius": 0.64 * mm});
            skLineSegment(sketch, "E32.28.0.24", {"start": v(-42.67, -49.73) * mm, "end": v(-39.12, -49.73) * mm, "construction": true});
            skCircle(sketch, "E32.28.0.25", {"center": v(-39.12, -49.73) * mm, "radius": 0.64 * mm});
            skCircle(sketch, "E32.29.0.0", {"center": v(39.12, -53.4) * mm, "radius": 0.64 * mm});
            skCircle(sketch, "E32.29.0.1", {"center": v(14.22, -53.4) * mm, "radius": 0.64 * mm});
            skCircle(sketch, "E32.29.0.2", {"center": v(-32, -53.4) * mm, "radius": 0.64 * mm});
            skCircle(sketch, "E32.29.0.3", {"center": v(10.67, -53.4) * mm, "radius": 0.64 * mm});
            skCircle(sketch, "E32.29.0.4", {"center": v(-35.56, -53.4) * mm, "radius": 0.64 * mm});
            skCircle(sketch, "E32.29.0.5", {"center": v(17.78, -53.4) * mm, "radius": 0.64 * mm});
            skCircle(sketch, "E32.29.0.6", {"center": v(3.56, -53.4) * mm, "radius": 0.64 * mm});
            skCircle(sketch, "E32.29.0.7", {"center": v(21.34, -53.4) * mm, "radius": 0.64 * mm});
            skCircle(sketch, "E32.29.0.8", {"center": v(42.67, -53.4) * mm, "radius": 0.64 * mm});
            skCircle(sketch, "E32.29.0.9", {"center": v(-7.11, -53.4) * mm, "radius": 0.64 * mm});
            skCircle(sketch, "E32.29.0.10", {"center": v(-3.56, -53.4) * mm, "radius": 0.64 * mm});
            skCircle(sketch, "E32.29.0.11", {"center": v(-10.67, -53.4) * mm, "radius": 0.64 * mm});
            skCircle(sketch, "E32.29.0.12", {"center": v(-14.22, -53.4) * mm, "radius": 0.64 * mm});
            skCircle(sketch, "E32.29.0.13", {"center": v(-21.34, -53.4) * mm, "radius": 0.64 * mm});
            skCircle(sketch, "E32.29.0.14", {"center": v(-24.9, -53.4) * mm, "radius": 0.64 * mm});
            skCircle(sketch, "E32.29.0.15", {"center": v(-28.45, -53.4) * mm, "radius": 0.64 * mm});
            skCircle(sketch, "E32.29.0.16", {"center": v(28.45, -53.4) * mm, "radius": 0.64 * mm});
            skCircle(sketch, "E32.29.0.17", {"center": v(7.11, -53.4) * mm, "radius": 0.64 * mm});
            skCircle(sketch, "E32.29.0.18", {"center": v(32, -53.4) * mm, "radius": 0.64 * mm});
            skCircle(sketch, "E32.29.0.19", {"center": v(35.56, -53.4) * mm, "radius": 0.64 * mm});
            skCircle(sketch, "E32.29.0.20", {"center": v(-17.78, -53.4) * mm, "radius": 0.64 * mm});
            skCircle(sketch, "E32.29.0.21", {"center": v(0, -53.4) * mm, "radius": 0.64 * mm});
            skCircle(sketch, "E32.29.0.22", {"center": v(24.9, -53.4) * mm, "radius": 0.64 * mm});
            skCircle(sketch, "E32.29.0.23", {"center": v(-42.67, -53.4) * mm, "radius": 0.64 * mm});
            skLineSegment(sketch, "E32.29.0.24", {"start": v(-42.67, -53.4) * mm, "end": v(-39.12, -53.4) * mm, "construction": true});
            skCircle(sketch, "E32.29.0.25", {"center": v(-39.12, -53.4) * mm, "radius": 0.64 * mm});
            skLineSegment(sketch, "E32.direction1", {"start": v(-42.67, 52.68) * mm, "end": v(-42.67, 49.02) * mm, "construction": true});
            skSolve(sketch);
        }
        {
            var Q0;
            Q0=makeQuery(id+"F1.opExtrude","CAP_FACE",FACE,{"disambiguationData":[OSD([sQuery(id+"F0.wireOp",EDGE,"7e58dfbd-d96a-4cb8-ae05-f5717cad55f7"),sQuery(id+"F0.wireOp",EDGE,"be0bfd59-5de7-4c36-b741-230e249a2633"),sQuery(id+"F0.wireOp",EDGE,"03ce3f70-f8f5-48b6-817a-86b3da3b079a"),sQuery(id+"F0.wireOp",EDGE,"bf2bad3a-775d-4bb9-9518-0aa501403ff7"),sQuery(id+"F0.wireOp",EDGE,"74c69ee1-55aa-481c-bcd1-1569f91f6e900.MirrorCS")])],"isStart":false});
            var Q1;
            {var subQ0=sQuery(id+"F0.wireOp",EDGE,"7e58dfbd-d96a-4cb8-ae05-f5717cad55f7");Q1=makeQuery(id+"F2.opFillet","BLEND_FACE",FACE,{"disambiguationData":[OSD([subQ0]),TDD([makeQuery(id+"F1.opExtrude","CAP_EDGE",EDGE,{"disambiguationData":[OSD([subQ0])],"isStart":false})])]});}
            var Q2;
            {var subQ0=sQuery(id+"F0.wireOp",EDGE,"be0bfd59-5de7-4c36-b741-230e249a2633");Q2=makeQuery(id+"F2.opFillet","BLEND_FACE",FACE,{"disambiguationData":[OSD([subQ0]),TDD([makeQuery(id+"F1.opExtrude","CAP_EDGE",EDGE,{"disambiguationData":[OSD([subQ0])],"isStart":false})])]});}
            var Q3;
            {var subQ0=sQuery(id+"F0.wireOp",EDGE,"be0bfd59-5de7-4c36-b741-230e249a2633");var subQ1=sQuery(id+"F0.wireOp",EDGE,"7e58dfbd-d96a-4cb8-ae05-f5717cad55f7");Q3=makeQuery(id+"F2.opFillet","BLEND_FACE",FACE,{"disambiguationData":[OSD([subQ1,subQ0]),TDD([makeQuery(id+"F1.opExtrude","CAP_VERTEX",VERTEX,{"disambiguationData":[OSD([subQ1,subQ0])],"isStart":false})])]});}
            var Q4;
            {var subQ0=sQuery(id+"F0.wireOp",EDGE,"03ce3f70-f8f5-48b6-817a-86b3da3b079a");var subQ1=sQuery(id+"F0.wireOp",EDGE,"be0bfd59-5de7-4c36-b741-230e249a2633");Q4=makeQuery(id+"F2.opFillet","BLEND_FACE",FACE,{"disambiguationData":[OSD([subQ1,subQ0]),TDD([makeQuery(id+"F1.opExtrude","CAP_VERTEX",VERTEX,{"disambiguationData":[OSD([subQ1,subQ0])],"isStart":false})])]});}
            var Q5;
            {var subQ0=sQuery(id+"F0.wireOp",EDGE,"03ce3f70-f8f5-48b6-817a-86b3da3b079a");Q5=makeQuery(id+"F2.opFillet","BLEND_FACE",FACE,{"disambiguationData":[OSD([subQ0]),TDD([makeQuery(id+"F1.opExtrude","CAP_EDGE",EDGE,{"disambiguationData":[OSD([subQ0])],"isStart":false})])]});}
            var Q6;
            {var subQ0=sQuery(id+"F0.wireOp",EDGE,"bf2bad3a-775d-4bb9-9518-0aa501403ff7");var subQ1=sQuery(id+"F0.wireOp",EDGE,"7e58dfbd-d96a-4cb8-ae05-f5717cad55f7");var subQ2=sQuery(id+"F0.wireOp",EDGE,"c97fd30b-f4b9-4084-8bae-b5abf99d8afd.top");Q6=makeQuery(id+"F2.opFillet","BLEND_FACE",FACE,{"disambiguationData":[OSD([subQ2,subQ1,subQ0]),TDD([makeQuery(id+"F1.opExtrude","CAP_VERTEX",VERTEX,{"disambiguationData":[OSD([subQ2,subQ1,subQ0])],"isStart":false})])]});}
            var Q7;
            Q7=makeQuery(id+"F2.opFillet","BLEND_FACE",FACE,{"disambiguationData":[OSD([sQuery(id+"F0.wireOp",EDGE,"bf2bad3a-775d-4bb9-9518-0aa501403ff7")])]});
            var Q8;
            {var subQ0=sQuery(id+"F0.wireOp",EDGE,"74c69ee1-55aa-481c-bcd1-1569f91f6e900.MirrorCS");var subQ1=sQuery(id+"F0.wireOp",EDGE,"03ce3f70-f8f5-48b6-817a-86b3da3b079a");var subQ2=sQuery(id+"F0.wireOp",EDGE,"c97fd30b-f4b9-4084-8bae-b5abf99d8afd.top");Q8=makeQuery(id+"F2.opFillet","BLEND_FACE",FACE,{"disambiguationData":[OSD([subQ2,subQ1,subQ0]),TDD([makeQuery(id+"F1.opExtrude","CAP_VERTEX",VERTEX,{"disambiguationData":[OSD([subQ2,subQ1,subQ0])],"isStart":false})])]});}
            var Q9;
            {var subQ0=sQuery(id+"F0.wireOp",EDGE,"74c69ee1-55aa-481c-bcd1-1569f91f6e900.MirrorCS");Q9=makeQuery(id+"F2.opFillet","BLEND_FACE",FACE,{"disambiguationData":[OSD([subQ0]),TDD([makeQuery(id+"F1.opExtrude","CAP_EDGE",EDGE,{"disambiguationData":[OSD([subQ0])],"isStart":false})])]});}
            var Q10;
            Q10=makeQuery(id+"F1.opExtrude","CAP_FACE",FACE,{"disambiguationData":[OSD([sQuery(id+"F0.wireOp",EDGE,"E12"),sQuery(id+"F0.wireOp",EDGE,"E13"),sQuery(id+"F0.wireOp",EDGE,"E14"),sQuery(id+"F0.wireOp",EDGE,"E15"),sQuery(id+"F0.wireOp",EDGE,"E16.MirrorCS")])],"isStart":true});
            var Q11;
            {var subQ0=sQuery(id+"F0.wireOp",EDGE,"E16.MirrorCS");var subQ1=sQuery(id+"F0.wireOp",EDGE,"E15");Q11=makeQuery(id+"F2.opFillet","BLEND_FACE",FACE,{"disambiguationData":[OSD([subQ1,subQ0]),TDD([makeQuery(id+"F1.opExtrude","CAP_EDGE",EDGE,{"disambiguationData":[OSD([subQ1,subQ0])],"isStart":true})])]});}
            var Q12;
            {var subQ0=sQuery(id+"F0.wireOp",EDGE,"E14");Q12=makeQuery(id+"F2.opFillet","BLEND_FACE",FACE,{"disambiguationData":[OSD([subQ0]),TDD([makeQuery(id+"F1.opExtrude","CAP_EDGE",EDGE,{"disambiguationData":[OSD([subQ0])],"isStart":true})])]});}
            var Q13;
            {var subQ0=sQuery(id+"F0.wireOp",EDGE,"E12");Q13=makeQuery(id+"F2.opFillet","BLEND_FACE",FACE,{"disambiguationData":[OSD([subQ0]),TDD([makeQuery(id+"F1.opExtrude","CAP_EDGE",EDGE,{"disambiguationData":[OSD([subQ0])],"isStart":true})])]});}
            var Q14;
            {var subQ0=sQuery(id+"F0.wireOp",EDGE,"E15");var subQ1=sQuery(id+"F0.wireOp",EDGE,"E12");var subQ2=sQuery(id+"F0.wireOp",EDGE,"E0.top");Q14=makeQuery(id+"F2.opFillet","BLEND_FACE",FACE,{"disambiguationData":[OSD([subQ2,subQ1,subQ0]),TDD([makeQuery(id+"F1.opExtrude","CAP_VERTEX",VERTEX,{"disambiguationData":[OSD([subQ2,subQ1,subQ0])],"isStart":true})])]});}
            var Q15;
            {var subQ0=sQuery(id+"F0.wireOp",EDGE,"E16.MirrorCS");var subQ1=sQuery(id+"F0.wireOp",EDGE,"E14");var subQ2=sQuery(id+"F0.wireOp",EDGE,"E0.top");Q15=makeQuery(id+"F2.opFillet","BLEND_FACE",FACE,{"disambiguationData":[OSD([subQ2,subQ1,subQ0]),TDD([makeQuery(id+"F1.opExtrude","CAP_VERTEX",VERTEX,{"disambiguationData":[OSD([subQ2,subQ1,subQ0])],"isStart":true})])]});}
            var Q16;
            {var subQ0=sQuery(id+"F0.wireOp",EDGE,"E13");Q16=makeQuery(id+"F2.opFillet","BLEND_FACE",FACE,{"disambiguationData":[OSD([subQ0]),TDD([makeQuery(id+"F1.opExtrude","CAP_EDGE",EDGE,{"disambiguationData":[OSD([subQ0])],"isStart":true})])]});}
            var Q17;
            {var subQ0=sQuery(id+"F0.wireOp",EDGE,"E13");var subQ1=sQuery(id+"F0.wireOp",EDGE,"E12");Q17=makeQuery(id+"F2.opFillet","BLEND_FACE",FACE,{"disambiguationData":[OSD([subQ1,subQ0]),TDD([makeQuery(id+"F1.opExtrude","CAP_VERTEX",VERTEX,{"disambiguationData":[OSD([subQ1,subQ0])],"isStart":true})])]});}
            var Q18;
            {var subQ0=sQuery(id+"F0.wireOp",EDGE,"E14");var subQ1=sQuery(id+"F0.wireOp",EDGE,"E13");Q18=makeQuery(id+"F2.opFillet","BLEND_FACE",FACE,{"disambiguationData":[OSD([subQ1,subQ0]),TDD([makeQuery(id+"F1.opExtrude","CAP_VERTEX",VERTEX,{"disambiguationData":[OSD([subQ1,subQ0])],"isStart":true})])]});}
            var Q19;
            Q19=makeQuery(id+"F1.opExtrude","CAP_FACE",FACE,{"disambiguationData":[OSD([sQuery(id+"F0.wireOp",EDGE,"E12"),sQuery(id+"F0.wireOp",EDGE,"E21"),sQuery(id+"F0.wireOp",EDGE,"E14"),sQuery(id+"F0.wireOp",EDGE,"E22"),sQuery(id+"F0.wireOp",EDGE,"E23.MirrorCS"),sQuery(id+"F0.wireOp",EDGE,"E24"),sQuery(id+"F0.wireOp",EDGE,"E25.MirrorCS"),sQuery(id+"F0.wireOp",EDGE,"E26")])],"isStart":false});
            var Q20;
            {var subQ0=sQuery(id+"F0.wireOp",EDGE,"E23.MirrorCS");Q20=makeQuery(id+"F2.opFillet","BLEND_FACE",FACE,{"disambiguationData":[OSD([subQ0]),TDD([makeQuery(id+"F1.opExtrude","CAP_EDGE",EDGE,{"disambiguationData":[OSD([subQ0])],"isStart":false})])]});}
            var Q21;
            {var subQ0=sQuery(id+"F0.wireOp",EDGE,"E25.MirrorCS");var subQ1=sQuery(id+"F0.wireOp",EDGE,"E23.MirrorCS");var subQ2=sQuery(id+"F0.wireOp",EDGE,"E18");Q21=makeQuery(id+"F2.opFillet","BLEND_FACE",FACE,{"disambiguationData":[OSD([subQ2,subQ1,subQ0]),TDD([makeQuery(id+"F1.opExtrude","CAP_VERTEX",VERTEX,{"disambiguationData":[OSD([subQ2,subQ1,subQ0])],"isStart":false})])]});}
            var Q22;
            {var subQ0=sQuery(id+"F0.wireOp",EDGE,"E25.MirrorCS");Q22=makeQuery(id+"F2.opFillet","BLEND_FACE",FACE,{"disambiguationData":[OSD([subQ0]),TDD([makeQuery(id+"F1.opExtrude","CAP_EDGE",EDGE,{"disambiguationData":[OSD([subQ0])],"isStart":false})])]});}
            var Q23;
            {var subQ0=sQuery(id+"F0.wireOp",EDGE,"E26");Q23=makeQuery(id+"F2.opFillet","BLEND_FACE",FACE,{"disambiguationData":[OSD([subQ0]),TDD([makeQuery(id+"F1.opExtrude","CAP_EDGE",EDGE,{"disambiguationData":[OSD([subQ0])],"isStart":false})])]});}
            var Q24;
            {var subQ0=sQuery(id+"F0.wireOp",EDGE,"E26");var subQ1=sQuery(id+"F0.wireOp",EDGE,"E25.MirrorCS");Q24=makeQuery(id+"F2.opFillet","BLEND_FACE",FACE,{"disambiguationData":[OSD([subQ1,subQ0]),TDD([makeQuery(id+"F1.opExtrude","CAP_VERTEX",VERTEX,{"disambiguationData":[OSD([subQ1,subQ0])],"isStart":false})])]});}
            var Q25;
            {var subQ0=sQuery(id+"F0.wireOp",EDGE,"E24");Q25=makeQuery(id+"F2.opFillet","BLEND_FACE",FACE,{"disambiguationData":[OSD([subQ0]),TDD([makeQuery(id+"F1.opExtrude","CAP_EDGE",EDGE,{"disambiguationData":[OSD([subQ0])],"isStart":false})])]});}
            var Q26;
            {var subQ0=sQuery(id+"F0.wireOp",EDGE,"E24");var subQ1=sQuery(id+"F0.wireOp",EDGE,"E22");var subQ2=sQuery(id+"F0.wireOp",EDGE,"E18");Q26=makeQuery(id+"F2.opFillet","BLEND_FACE",FACE,{"disambiguationData":[OSD([subQ2,subQ1,subQ0]),TDD([makeQuery(id+"F1.opExtrude","CAP_VERTEX",VERTEX,{"disambiguationData":[OSD([subQ2,subQ1,subQ0])],"isStart":false})])]});}
            var Q27;
            {var subQ0=sQuery(id+"F0.wireOp",EDGE,"E26");var subQ1=sQuery(id+"F0.wireOp",EDGE,"E24");Q27=makeQuery(id+"F2.opFillet","BLEND_FACE",FACE,{"disambiguationData":[OSD([subQ1,subQ0]),TDD([makeQuery(id+"F1.opExtrude","CAP_VERTEX",VERTEX,{"disambiguationData":[OSD([subQ1,subQ0])],"isStart":false})])]});}
            var Q28;
            {var subQ0=sQuery(id+"F0.wireOp",EDGE,"E22");Q28=makeQuery(id+"F2.opFillet","BLEND_FACE",FACE,{"disambiguationData":[OSD([subQ0]),TDD([makeQuery(id+"F1.opExtrude","CAP_EDGE",EDGE,{"disambiguationData":[OSD([subQ0])],"isStart":false})])]});}
            var Q29;
            {var subQ0=sQuery(id+"F0.wireOp",EDGE,"E12");Q29=makeQuery(id+"F2.opFillet","BLEND_FACE",FACE,{"disambiguationData":[OSD([subQ0]),TDD([makeQuery(id+"F1.opExtrude","CAP_EDGE",EDGE,{"disambiguationData":[OSD([subQ0])],"isStart":false})])]});}
            var Q30;
            {var subQ0=sQuery(id+"F0.wireOp",EDGE,"E22");var subQ1=sQuery(id+"F0.wireOp",EDGE,"E12");var subQ2=sQuery(id+"F0.wireOp",EDGE,"E0.top");Q30=makeQuery(id+"F2.opFillet","BLEND_FACE",FACE,{"disambiguationData":[OSD([subQ2,subQ1,subQ0]),TDD([makeQuery(id+"F1.opExtrude","CAP_VERTEX",VERTEX,{"disambiguationData":[OSD([subQ2,subQ1,subQ0])],"isStart":false})])]});}
            var Q31;
            {var subQ0=sQuery(id+"F0.wireOp",EDGE,"E21");var subQ1=sQuery(id+"F0.wireOp",EDGE,"E12");Q31=makeQuery(id+"F2.opFillet","BLEND_FACE",FACE,{"disambiguationData":[OSD([subQ1,subQ0]),TDD([makeQuery(id+"F1.opExtrude","CAP_VERTEX",VERTEX,{"disambiguationData":[OSD([subQ1,subQ0])],"isStart":false})])]});}
            var Q32;
            {var subQ0=sQuery(id+"F0.wireOp",EDGE,"E21");Q32=makeQuery(id+"F2.opFillet","BLEND_FACE",FACE,{"disambiguationData":[OSD([subQ0]),TDD([makeQuery(id+"F1.opExtrude","CAP_EDGE",EDGE,{"disambiguationData":[OSD([subQ0])],"isStart":false})])]});}
            var Q33;
            {var subQ0=sQuery(id+"F0.wireOp",EDGE,"E14");var subQ1=sQuery(id+"F0.wireOp",EDGE,"E21");Q33=makeQuery(id+"F2.opFillet","BLEND_FACE",FACE,{"disambiguationData":[OSD([subQ1,subQ0]),TDD([makeQuery(id+"F1.opExtrude","CAP_VERTEX",VERTEX,{"disambiguationData":[OSD([subQ1,subQ0])],"isStart":false})])]});}
            var Q34;
            {var subQ0=sQuery(id+"F0.wireOp",EDGE,"E14");Q34=makeQuery(id+"F2.opFillet","BLEND_FACE",FACE,{"disambiguationData":[OSD([subQ0]),TDD([makeQuery(id+"F1.opExtrude","CAP_EDGE",EDGE,{"disambiguationData":[OSD([subQ0])],"isStart":false})])]});}
            var Q35;
            {var subQ0=sQuery(id+"F0.wireOp",EDGE,"E23.MirrorCS");var subQ1=sQuery(id+"F0.wireOp",EDGE,"E14");var subQ2=sQuery(id+"F0.wireOp",EDGE,"E0.top");Q35=makeQuery(id+"F2.opFillet","BLEND_FACE",FACE,{"disambiguationData":[OSD([subQ2,subQ1,subQ0]),TDD([makeQuery(id+"F1.opExtrude","CAP_VERTEX",VERTEX,{"disambiguationData":[OSD([subQ2,subQ1,subQ0])],"isStart":false})])]});}
            shell(context, id + "F4", {"entities" : qUnion([Q0, Q1, Q2, Q3, Q4, Q5, Q6, Q7, Q8, Q9, Q10, Q11, Q12, Q13, Q14, Q15, Q16, Q17, Q18, Q19, Q20, Q21, Q22, Q23, Q24, Q25, Q26, Q27, Q28, Q29, Q30, Q31, Q32, Q33, Q34, Q35]), "thickness" : 2.54 * mm});
        }
        {
            var Q0;
            Q0 = qSketchRegion(id + "F3", true);
            extrude(context, id + "F5", {"entities" : qUnion([Q0]), "operationType" : NewBodyOperationType.REMOVE, "depth" : 25.4 * mm, "offsetDistance" : 25.4 * mm});
        }
        {
            var Q0;
            Q0=makeQuery(id+"F1.opExtrude","SWEPT_BODY",BODY,{"disambiguationData":[OSD([sQuery(id+"F0.wireOp",EDGE,"E12"),sQuery(id+"F0.wireOp",EDGE,"E21"),sQuery(id+"F0.wireOp",EDGE,"E14"),sQuery(id+"F0.wireOp",EDGE,"E22"),sQuery(id+"F0.wireOp",EDGE,"E23.MirrorCS"),sQuery(id+"F0.wireOp",EDGE,"E24"),sQuery(id+"F0.wireOp",EDGE,"E25.MirrorCS"),sQuery(id+"F0.wireOp",EDGE,"E26")])]});
            transform(context, id + "F6", {"entities" : qUnion([Q0]), "transformType" : TransformType.TRANSLATION_3D, "dx" : 0 * mm, "dy" : 151.9 * mm, "dz" : 0 * mm, "makeCopy" : false});
        }
        {
            var Q0;
            Q0=qCreatedBy(makeId("Front.planeOp"),FACE);
            var sketch = newSketch(context, id + "F7", { "sketchPlane" : qUnion([Q0])});
            skLineSegment(sketch, "E33.bottom", {"start": v(-18.04, 15.43) * mm, "end": v(18.03, 15.43) * mm});
            skLineSegment(sketch, "E33.top", {"start": v(-18.04, 10.8) * mm, "end": v(18.03, 10.8) * mm});
            skLineSegment(sketch, "E33.left", {"start": v(-18.04, 15.43) * mm, "end": v(-18.04, 10.8) * mm});
            skLineSegment(sketch, "E33.right", {"start": v(18.03, 15.43) * mm, "end": v(18.03, 10.8) * mm});
            skSolve(sketch);
        }
        {
            var Q0;
            Q0 = qSketchRegion(id + "F7", true);
            extrude(context, id + "F8", {"entities" : qUnion([Q0]), "operationType" : NewBodyOperationType.REMOVE, "depth" : 25.4 * mm, "offsetDistance" : 25.4 * mm});
        }
    });
